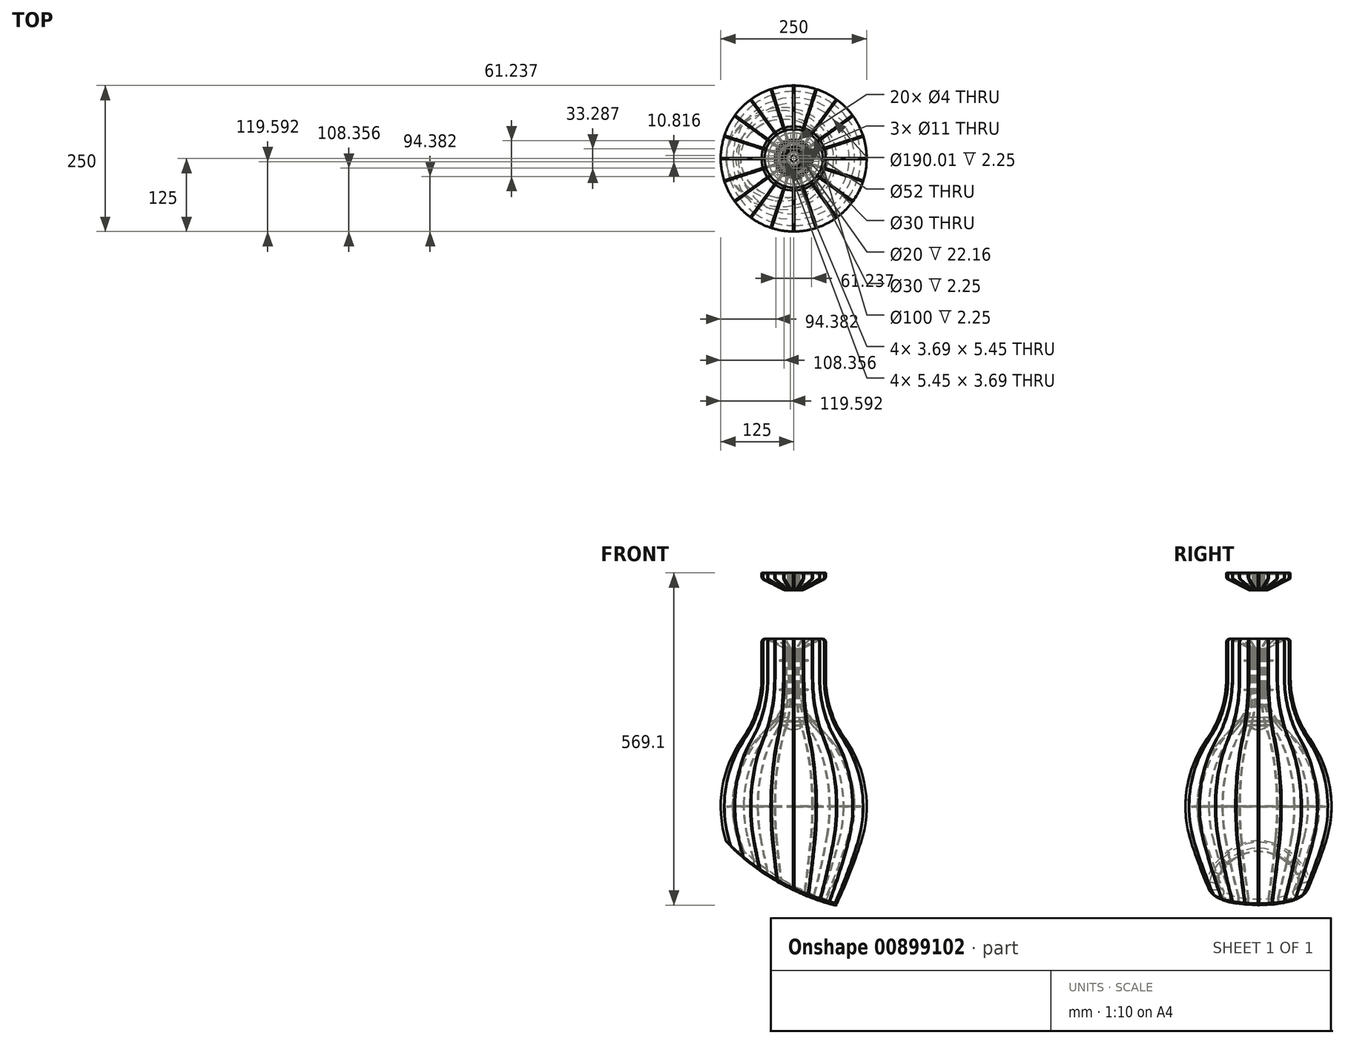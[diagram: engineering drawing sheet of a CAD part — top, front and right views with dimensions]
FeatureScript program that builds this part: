
annotation { "Feature Type Name" : "Feature", "Feature Type Description" : "" }
export const myFeature = defineFeature(function(context is Context, id is Id, definition is map)
    precondition{}
    {
        {
            assignVariable(context, id + "F0", {"variableType" : VariableType.LENGTH, "name" : "t", "lengthValue" : 2.25 * mm});
        }
        {
            var Q0;
            Q0=qCreatedBy(makeId("Front.planeOp"),FACE);
            var sketch = newSketch(context, id + "F1", { "sketchPlane" : qUnion([Q0])});
            skArc(sketch, "E0", {"start": v(-88.23, 115.57) * mm, "mid": v(-122.8, 29.63) * mm, "end": v(-114.93, -62.67) * mm});
            skArc(sketch, "E1", {"start": v(-88.23, 115.57) * mm, "mid": v(-63.5, 165.2) * mm, "end": v(-55, 220) * mm});
            skLineSegment(sketch, "E2", {"start": v(0, 0) * mm, "end": v(0, 200) * mm, "construction": true});
            skArc(sketch, "E3", {"start": v(-44.38, 134.72) * mm, "mid": v(-22.68, 164.2) * mm, "end": v(-15, 200) * mm});
            skArc(sketch, "E4", {"start": v(-44.38, 134.72) * mm, "mid": v(-98.19, 49.04) * mm, "end": v(-97.29, -52.12) * mm});
            skLineSegment(sketch, "E5", {"start": v(-55, 220) * mm, "end": v(-55, 290) * mm});
            skLineSegment(sketch, "E6", {"start": v(-55, 290) * mm, "end": v(-15, 270) * mm});
            skLineSegment(sketch, "E7", {"start": v(-15, 200) * mm, "end": v(-15, 270) * mm});
            skArc(sketch, "E8", {"start": v(-114.93, -62.67) * mm, "mid": v(-65.32, -185.14) * mm, "end": v(0, -300) * mm});
            skArc(sketch, "E9", {"start": v(-97.29, -52.12) * mm, "mid": v(-56.14, -159.57) * mm, "end": v(0, -260) * mm});
            skLineSegment(sketch, "E10", {"start": v(0, -300) * mm, "end": v(0, -260) * mm});
            skLineSegment(sketch, "E11", {"start": v(-10, 367.5) * mm, "end": v(-55, 390) * mm});
            skLineSegment(sketch, "E12", {"start": v(-55, 390) * mm, "end": v(-55, 400) * mm});
            skLineSegment(sketch, "E13", {"start": v(-55, 400) * mm, "end": v(-50, 400) * mm});
            skLineSegment(sketch, "E14", {"start": v(-10, 397.75) * mm, "end": v(-10, 367.5) * mm});
            skLineSegment(sketch, "E15", {"start": v(-50, 400) * mm, "end": v(-50, 397.75) * mm});
            skLineSegment(sketch, "E16", {"start": v(-50, 397.75) * mm, "end": v(-20, 397.75) * mm});
            skLineSegment(sketch, "E17", {"start": v(-20, 397.75) * mm, "end": v(-20, 400) * mm});
            skLineSegment(sketch, "E18.trimOffspring", {"start": v(-20, 400) * mm, "end": v(-15, 400) * mm});
            skLineSegment(sketch, "E19", {"start": v(-15, 400) * mm, "end": v(-15, 397.75) * mm});
            skLineSegment(sketch, "E20", {"start": v(-15, 397.75) * mm, "end": v(-10, 397.75) * mm});
            skPoint(sketch, "E21.orphan", {"position": v(-10, 400) * mm});
            skSolve(sketch);
        }
        {
            var Q0;
            Q0 = qSketchRegion(id + "F1", true);
            var Q1;
            Q1=sQuery(id+"F1.wireOp",EDGE,"E2");
            revolve(context, id + "F2", {"surfaceOperationType" : NewSurfaceOperationType.NEW, "entities" : qUnion([Q0]), "axis" : qUnion([Q1]), "revolveType" : RevolveType.FULL});
        }
        {
            var Q0;
            Q0=qCreatedBy(makeId("Front.planeOp"),FACE);
            var sketch = newSketch(context, id + "F3", { "sketchPlane" : qUnion([Q0])});
            skLineSegment(sketch, "E22.bottom", {"start": v(-115.8, -300) * mm, "end": v(72.5, -300) * mm});
            skLineSegment(sketch, "E22.left", {"start": v(72.5, -300) * mm, "end": v(72.5, -170) * mm});
            skLineSegment(sketch, "E22.right", {"start": v(-115.8, -300) * mm, "end": v(-115.8, -60) * mm});
            skLineSegment(sketch, "E23", {"start": v(0, 0) * mm, "end": v(0, -300) * mm, "construction": true});
            skPoint(sketch, "E24", {"position": v(-115.8, -60) * mm});
            skArc(sketch, "E25.converted", {"start": v(-115.8, -60) * mm, "mid": v(-29.3, -128.08) * mm, "end": v(72.5, -170) * mm});
            skLineSegment(sketch, "E26", {"start": v(72.5, -170) * mm, "end": v(-115.8, -170) * mm, "construction": true});
            skArc(sketch, "E27", {"start": v(0, -300) * mm, "mid": v(-65.32, -185.14) * mm, "end": v(-114.93, -62.67) * mm, "construction": true});
            skArc(sketch, "E28", {"start": v(114.93, -62.67) * mm, "mid": v(65.32, -185.14) * mm, "end": v(0, -300) * mm, "construction": true});
            skSolve(sketch);
        }
        {
            var Q0;
            Q0 = qSketchRegion(id + "F3", true);
            extrude(context, id + "F4", {"entities" : qUnion([Q0]), "operationType" : NewBodyOperationType.REMOVE, "depth" : 500 * mm, "offsetDistance" : 25 * mm, "symmetric" : true});
        }
        {
            var Q0;
            Q0=makeQuery(id+"F2.opRevolve","SWEPT_EDGE",EDGE,{"disambiguationData":[OSD([sQuery(id+"F1.wireOp",EDGE,"E5"),sQuery(id+"F1.wireOp",EDGE,"E6")])]});
            var Q1;
            Q1=makeQuery(id+"F2.opRevolve","SWEPT_EDGE",EDGE,{"disambiguationData":[OSD([sQuery(id+"F1.wireOp",EDGE,"E6"),sQuery(id+"F1.wireOp",EDGE,"E7")])]});
            var Q2;
            Q2=makeQuery(id+"F4.boolean.opBoolean","INTERSECT",EDGE,{"derivedFrom":[makeQuery(id+"F2.opRevolve","SWEPT_FACE",FACE,{"disambiguationData":[OSD([sQuery(id+"F1.wireOp",EDGE,"E8")])]}),makeQuery(id+"F4.opExtrude","SWEPT_FACE",FACE,{"disambiguationData":[OSD([sQuery(id+"F3.wireOp",EDGE,"E25.converted")])]})]});
            var Q3;
            Q3=makeQuery(id+"F4.boolean.opBoolean","INTERSECT",EDGE,{"derivedFrom":[makeQuery(id+"F2.opRevolve","SWEPT_FACE",FACE,{"disambiguationData":[OSD([sQuery(id+"F1.wireOp",EDGE,"E9")])]}),makeQuery(id+"F4.opExtrude","SWEPT_FACE",FACE,{"disambiguationData":[OSD([sQuery(id+"F3.wireOp",EDGE,"E25.converted")])]})]});
            var Q4;
            Q4=makeQuery(id+"F2.opRevolve","SWEPT_EDGE",EDGE,{"disambiguationData":[OSD([sQuery(id+"F1.wireOp",EDGE,"E11"),sQuery(id+"F1.wireOp",EDGE,"E14")])]});
            var Q5;
            Q5=makeQuery(id+"F2.opRevolve","SWEPT_EDGE",EDGE,{"disambiguationData":[OSD([sQuery(id+"F1.wireOp",EDGE,"E11"),sQuery(id+"F1.wireOp",EDGE,"E12")])]});
            fillet(context, id + "F5", {"entities" : qUnion([Q0, Q1, Q2, Q3, Q4, Q5]), "tangentPropagation" : true, "radius" : 5 * mm, "defaultsChanged" : false, "vertexSettings" : [], "allowEdgeOverflow" : false});
        }
        {
            var Q0;
            Q0=qCreatedBy(makeId("Front.planeOp"),FACE);
            var sketch = newSketch(context, id + "F6", { "sketchPlane" : qUnion([Q0])});
            skArc(sketch, "E29", {"start": v(-47.76, 286.38) * mm, "mid": v(-52.63, 286.16) * mm, "end": v(-55, 281.9) * mm});
            skArc(sketch, "E30", {"start": v(55, 281.9) * mm, "mid": v(52.63, 286.16) * mm, "end": v(47.76, 286.38) * mm});
            skLineSegment(sketch, "E31", {"start": v(55, 220) * mm, "end": v(55, 281.9) * mm});
            skLineSegment(sketch, "E32", {"start": v(-55, 281.9) * mm, "end": v(-55, 220) * mm});
            skArc(sketch, "E33", {"start": v(88.23, 115.57) * mm, "mid": v(63.5, 165.2) * mm, "end": v(55, 220) * mm});
            skArc(sketch, "E34", {"start": v(-55, 220) * mm, "mid": v(-63.5, 165.2) * mm, "end": v(-88.23, 115.57) * mm});
            skArc(sketch, "E35", {"start": v(88.23, 115.57) * mm, "mid": v(122.8, 29.63) * mm, "end": v(114.93, -62.67) * mm});
            skArc(sketch, "E36", {"start": v(-116.14, -58.88) * mm, "mid": v(-122.49, 31.6) * mm, "end": v(-88.23, 115.57) * mm});
            skArc(sketch, "E37", {"start": v(114.93, -62.67) * mm, "mid": v(96.03, -115) * mm, "end": v(74.26, -166.18) * mm});
            skArc(sketch, "E38", {"start": v(68.41, -168.92) * mm, "mid": v(71.84, -168.62) * mm, "end": v(74.26, -166.18) * mm});
            skArc(sketch, "E39", {"start": v(-99.56, -75.95) * mm, "mid": v(-107.36, -68.52) * mm, "end": v(-114.95, -60.88) * mm});
            skArc(sketch, "E40", {"start": v(68.41, -168.92) * mm, "mid": v(63.85, -167.67) * mm, "end": v(59.31, -166.36) * mm});
            skArc(sketch, "E41", {"start": v(56.2, -159.44) * mm, "mid": v(56.17, -163.61) * mm, "end": v(59.31, -166.36) * mm});
            skArc(sketch, "E42", {"start": v(-99.56, -75.95) * mm, "mid": v(-93.46, -76.5) * mm, "end": v(-91.41, -70.72) * mm});
            skArc(sketch, "E43", {"start": v(97.29, -52.12) * mm, "mid": v(78.67, -106.52) * mm, "end": v(56.2, -159.44) * mm});
            skArc(sketch, "E44", {"start": v(-91.41, -70.72) * mm, "mid": v(-94.4, -61.44) * mm, "end": v(-97.29, -52.12) * mm});
            skArc(sketch, "E45", {"start": v(44.38, 134.72) * mm, "mid": v(98.19, 49.04) * mm, "end": v(97.29, -52.12) * mm});
            skArc(sketch, "E46", {"start": v(-97.29, -52.12) * mm, "mid": v(-98.19, 49.04) * mm, "end": v(-44.38, 134.72) * mm});
            skArc(sketch, "E47", {"start": v(44.38, 134.72) * mm, "mid": v(22.68, 164.2) * mm, "end": v(15, 200) * mm});
            skArc(sketch, "E48", {"start": v(-15, 200) * mm, "mid": v(-22.68, 164.2) * mm, "end": v(-44.38, 134.72) * mm});
            skLineSegment(sketch, "E49", {"start": v(15, 200) * mm, "end": v(15, 266.9) * mm});
            skLineSegment(sketch, "E50", {"start": v(-15, 266.9) * mm, "end": v(-15, 200) * mm});
            skArc(sketch, "E51", {"start": v(-15, 266.9) * mm, "mid": v(-15.75, 269.54) * mm, "end": v(-17.76, 271.38) * mm});
            skArc(sketch, "E52", {"start": v(17.76, 271.38) * mm, "mid": v(15.75, 269.54) * mm, "end": v(15, 266.9) * mm});
            skLineSegment(sketch, "E53", {"start": v(-17.76, 271.38) * mm, "end": v(-47.76, 286.38) * mm});
            skLineSegment(sketch, "E54", {"start": v(47.76, 286.38) * mm, "end": v(17.76, 271.38) * mm});
            skArc(sketch, "E55", {"start": v(-116.14, -58.88) * mm, "mid": v(-115.66, -59.95) * mm, "end": v(-114.95, -60.88) * mm});
            skArc(sketch, "E56", {"start": v(-17.24, 371.12) * mm, "mid": v(-12.37, 371.34) * mm, "end": v(-10, 375.6) * mm});
            skLineSegment(sketch, "E57", {"start": v(-10, 375.6) * mm, "end": v(-10, 397.75) * mm});
            skLineSegment(sketch, "E58", {"start": v(-52.24, 388.62) * mm, "end": v(-17.24, 371.12) * mm});
            skArc(sketch, "E59", {"start": v(-55, 393.1) * mm, "mid": v(-54.25, 390.46) * mm, "end": v(-52.24, 388.62) * mm});
            skLineSegment(sketch, "E60", {"start": v(-55, 400) * mm, "end": v(-55, 393.1) * mm});
            skLineSegment(sketch, "E61", {"start": v(-50, 400) * mm, "end": v(-55, 400) * mm});
            skLineSegment(sketch, "E62", {"start": v(-20, 397.75) * mm, "end": v(-50, 397.75) * mm});
            skLineSegment(sketch, "E63", {"start": v(-15, 400) * mm, "end": v(-20, 400) * mm});
            skLineSegment(sketch, "E64", {"start": v(-10, 397.75) * mm, "end": v(-15, 397.75) * mm});
            skLineSegment(sketch, "E65", {"start": v(-15, 397.75) * mm, "end": v(-15, 400) * mm});
            skLineSegment(sketch, "E66", {"start": v(-20, 400) * mm, "end": v(-20, 397.75) * mm});
            skLineSegment(sketch, "E67", {"start": v(-50, 397.75) * mm, "end": v(-50, 400) * mm});
            skSolve(sketch);
        }
        {
            var Q0;
            Q0 = qSketchRegion(id + "F6", true);
            extrude(context, id + "F7", {"entities" : qUnion([Q0]), "depth" : getVariable(context, 't'), "offsetDistance" : 25 * mm, "symmetric" : true});
        }
        {
            var Q0;
            Q0=qCreatedBy(makeId("Front.planeOp"),FACE);
            var Q1;
            Q1=sQuery(id+"F3.wireOp",EDGE,"E23");
            cPlane(context, id + "F8", {"entities" : qUnion([Q0, Q1]), "cplaneType" : CPlaneType.LINE_ANGLE, "offset" : 25 * mm, "angle" : 18 * degree, "width" : 150 * mm, "height" : 150 * mm});
        }
        {
            var Q0;
            Q0=qCreatedBy(id+"F8.planeOp",FACE);
            var sketch = newSketch(context, id + "F9", { "sketchPlane" : qUnion([Q0])});
            skFitSpline(sketch, "E68", {"points": [v(-74.64, -165.34) * mm, v(-74.52, -165.6) * mm, v(-74.3, -165.99) * mm, v(-73.95, -166.45) * mm, v(-73.66, -166.78) * mm, v(-73.33, -167.08) * mm, v(-72.99, -167.35) * mm, v(-72.62, -167.59) * mm, v(-72.23, -167.8) * mm, v(-71.83, -167.97) * mm, v(-71.41, -168.1) * mm, v(-70.99, -168.2) * mm, v(-70.4, -168.28) * mm, v(-69.67, -168.28) * mm, v(-69.1, -168.19) * mm, v(-68.8, -168.1) * mm]});
            skFitSpline(sketch, "E69", {"points": [v(111.92, -69.42) * mm, v(112.28, -69.08) * mm, v(112.75, -68.51) * mm, v(113.24, -67.64) * mm, v(113.43, -67.18) * mm, v(113.5, -66.95) * mm]});
            skEllipticalArc(sketch, "E70", {});
            skEllipticalArc(sketch, "E71", {});
            skFitSpline(sketch, "E72", {"points": [v(89.43, -76.68) * mm, v(89.34, -76.94) * mm, v(89.2, -77.47) * mm, v(89.1, -78.3) * mm, v(89.13, -79.13) * mm, v(89.25, -79.8) * mm, v(89.4, -80.33) * mm, v(89.6, -80.85) * mm, v(89.86, -81.34) * mm, v(90.17, -81.8) * mm, v(90.44, -82.11) * mm, v(90.73, -82.4) * mm, v(91.04, -82.68) * mm, v(91.38, -82.92) * mm, v(91.74, -83.13) * mm, v(92.12, -83.3) * mm, v(92.5, -83.44) * mm, v(92.9, -83.55) * mm, v(93.31, -83.62) * mm, v(93.73, -83.65) * mm, v(94.14, -83.65) * mm, v(94.55, -83.61) * mm, v(95.1, -83.5) * mm, v(95.76, -83.3) * mm, v(96.5, -82.93) * mm, v(96.96, -82.6) * mm, v(97.17, -82.42) * mm]});
            skFitSpline(sketch, "E73", {"points": [v(-59.7, -165.6) * mm, v(-59.35, -165.5) * mm, v(-58.85, -165.3) * mm, v(-58.24, -164.92) * mm, v(-57.8, -164.58) * mm, v(-57.42, -164.2) * mm, v(-57.07, -163.8) * mm, v(-56.77, -163.34) * mm, v(-56.52, -162.86) * mm, v(-56.33, -162.36) * mm, v(-56.14, -161.65) * mm, v(-56.07, -160.94) * mm, v(-56.11, -160.21) * mm, v(-56.2, -159.68) * mm, v(-56.35, -159.16) * mm, v(-56.48, -158.83) * mm, v(-56.56, -158.66) * mm]});
            skArc(sketch, "E74", {"start": v(114.93, -62.67) * mm, "mid": v(114.22, -64.81) * mm, "end": v(113.5, -66.95) * mm});
            skArc(sketch, "E75", {"start": v(-74.64, -165.34) * mm, "mid": v(-96.2, -114.56) * mm, "end": v(-114.93, -62.67) * mm});
            skArc(sketch, "E76", {"start": v(88.23, 115.57) * mm, "mid": v(122.8, 29.63) * mm, "end": v(114.93, -62.67) * mm});
            skArc(sketch, "E77", {"start": v(-114.93, -62.67) * mm, "mid": v(-122.8, 29.63) * mm, "end": v(-88.23, 115.57) * mm});
            skArc(sketch, "E78", {"start": v(44.38, 134.72) * mm, "mid": v(98.19, 49.04) * mm, "end": v(97.29, -52.12) * mm});
            skArc(sketch, "E79", {"start": v(-97.29, -52.12) * mm, "mid": v(-98.19, 49.04) * mm, "end": v(-44.38, 134.72) * mm});
            skArc(sketch, "E80", {"start": v(97.29, -52.12) * mm, "mid": v(93.46, -64.43) * mm, "end": v(89.43, -76.68) * mm});
            skArc(sketch, "E81", {"start": v(-56.56, -158.66) * mm, "mid": v(-78.83, -106.12) * mm, "end": v(-97.29, -52.12) * mm});
            skArc(sketch, "E82", {"start": v(88.23, 115.57) * mm, "mid": v(63.5, 165.2) * mm, "end": v(55, 220) * mm});
            skArc(sketch, "E83", {"start": v(-55, 220) * mm, "mid": v(-63.5, 165.2) * mm, "end": v(-88.23, 115.57) * mm});
            skLineSegment(sketch, "E84", {"start": v(55, 220) * mm, "end": v(55, 281.9) * mm});
            skLineSegment(sketch, "E85", {"start": v(-55, 281.9) * mm, "end": v(-55, 220) * mm});
            skArc(sketch, "E86", {"start": v(-47.76, 286.38) * mm, "mid": v(-52.63, 286.16) * mm, "end": v(-55, 281.9) * mm});
            skArc(sketch, "E87", {"start": v(55, 281.9) * mm, "mid": v(52.63, 286.16) * mm, "end": v(47.76, 286.38) * mm});
            skLineSegment(sketch, "E88", {"start": v(-17.76, 271.38) * mm, "end": v(-47.76, 286.38) * mm});
            skLineSegment(sketch, "E89", {"start": v(47.76, 286.38) * mm, "end": v(17.76, 271.38) * mm});
            skArc(sketch, "E90", {"start": v(-15, 266.9) * mm, "mid": v(-15.75, 269.54) * mm, "end": v(-17.76, 271.38) * mm});
            skArc(sketch, "E91", {"start": v(17.76, 271.38) * mm, "mid": v(15.75, 269.54) * mm, "end": v(15, 266.9) * mm});
            skLineSegment(sketch, "E92", {"start": v(15, 200) * mm, "end": v(15, 266.9) * mm});
            skLineSegment(sketch, "E93", {"start": v(-15, 266.9) * mm, "end": v(-15, 200) * mm});
            skArc(sketch, "E94", {"start": v(44.38, 134.72) * mm, "mid": v(22.68, 164.2) * mm, "end": v(15, 200) * mm});
            skArc(sketch, "E95", {"start": v(-15, 200) * mm, "mid": v(-22.68, 164.2) * mm, "end": v(-44.38, 134.72) * mm});
            const initialGuessF9  = {"E70": [-0.18134494701990392, 0.217305327537415, 1, 0, 0.4205848896953069, 0.4, 4.98326227178671, 5.0058128826202495], "E71": [-0.18134494701990392, 0.217305327537415, 1, 0, 0.4205848896953069, 0.4, 5.436156316925889, 5.4839668003792745]};
            skSetInitialGuess(sketch, initialGuessF9);
            skSolve(sketch);
        }
        {
            var Q0;
            Q0 = qSketchRegion(id + "F9", true);
            extrude(context, id + "F10", {"entities" : qUnion([Q0]), "depth" : getVariable(context, 't'), "offsetDistance" : 25 * mm, "symmetric" : true});
        }
        {
            var Q0;
            Q0=qCreatedBy(makeId("Front.planeOp"),FACE);
            var Q1;
            Q1=sQuery(id+"F3.wireOp",EDGE,"E23");
            cPlane(context, id + "F11", {"entities" : qUnion([Q0, Q1]), "cplaneType" : CPlaneType.LINE_ANGLE, "offset" : 25 * mm, "angle" : 36 * degree, "width" : 150 * mm, "height" : 150 * mm});
        }
        {
            var Q0;
            Q0=qCreatedBy(id+"F11.planeOp",FACE);
            var sketch = newSketch(context, id + "F12", { "sketchPlane" : qUnion([Q0])});
            skArc(sketch, "E96", {"start": v(-47.76, 286.38) * mm, "mid": v(-52.63, 286.16) * mm, "end": v(-55, 281.9) * mm});
            skArc(sketch, "E97", {"start": v(55, 281.9) * mm, "mid": v(52.63, 286.16) * mm, "end": v(47.76, 286.38) * mm});
            skLineSegment(sketch, "E98", {"start": v(55, 220) * mm, "end": v(55, 281.9) * mm});
            skLineSegment(sketch, "E99", {"start": v(-55, 281.9) * mm, "end": v(-55, 220) * mm});
            skArc(sketch, "E100", {"start": v(88.23, 115.57) * mm, "mid": v(63.5, 165.2) * mm, "end": v(55, 220) * mm});
            skArc(sketch, "E101", {"start": v(-55, 220) * mm, "mid": v(-63.5, 165.2) * mm, "end": v(-88.23, 115.57) * mm});
            skArc(sketch, "E102", {"start": v(88.23, 115.57) * mm, "mid": v(122.8, 29.63) * mm, "end": v(114.93, -62.67) * mm});
            skArc(sketch, "E103", {"start": v(-114.93, -62.67) * mm, "mid": v(-122.8, 29.63) * mm, "end": v(-88.23, 115.57) * mm});
            skArc(sketch, "E104", {"start": v(114.93, -62.67) * mm, "mid": v(111, -74.3) * mm, "end": v(106.95, -85.88) * mm});
            skArc(sketch, "E105", {"start": v(-75.84, -162.71) * mm, "mid": v(-96.73, -113.22) * mm, "end": v(-114.93, -62.67) * mm});
            skFitSpline(sketch, "E106", {"points": [v(-75.84, -162.71) * mm, v(-75.72, -162.98) * mm, v(-75.5, -163.36) * mm, v(-75.16, -163.83) * mm, v(-74.87, -164.16) * mm, v(-74.55, -164.46) * mm, v(-74.2, -164.73) * mm, v(-73.85, -164.98) * mm, v(-73.46, -165.2) * mm, v(-73.06, -165.37) * mm, v(-72.64, -165.5) * mm, v(-72.22, -165.61) * mm, v(-71.79, -165.68) * mm, v(-71.35, -165.71) * mm, v(-70.77, -165.7) * mm, v(-70.34, -165.64) * mm, v(-70.05, -165.57) * mm]});
            skFitSpline(sketch, "E107", {"points": [v(104.37, -89.28) * mm, v(104.68, -89.08) * mm, v(105.1, -88.74) * mm, v(105.6, -88.21) * mm, v(106.05, -87.65) * mm, v(106.53, -86.9) * mm, v(106.83, -86.23) * mm, v(106.95, -85.88) * mm]});
            skEllipticalArc(sketch, "E108", {});
            skEllipticalArc(sketch, "E109", {});
            skFitSpline(sketch, "E110", {"points": [v(84.35, -91.22) * mm, v(84.17, -91.73) * mm, v(83.98, -92.51) * mm, v(83.92, -93.45) * mm, v(83.94, -94) * mm, v(83.99, -94.53) * mm, v(84.11, -95.18) * mm, v(84.32, -95.82) * mm, v(84.55, -96.31) * mm, v(84.75, -96.66) * mm, v(84.97, -97) * mm, v(85.23, -97.31) * mm, v(85.51, -97.6) * mm, v(85.82, -97.87) * mm, v(86.14, -98.1) * mm, v(86.5, -98.3) * mm, v(86.87, -98.48) * mm, v(87.25, -98.6) * mm, v(87.64, -98.7) * mm, v(88.05, -98.76) * mm, v(88.45, -98.77) * mm, v(88.85, -98.75) * mm, v(89.26, -98.7) * mm, v(89.79, -98.58) * mm, v(90.42, -98.35) * mm, v(90.9, -98.1) * mm, v(91.13, -97.95) * mm]});
            skFitSpline(sketch, "E111", {"points": [v(-60.9, -163.25) * mm, v(-60.54, -163.16) * mm, v(-59.86, -162.9) * mm, v(-59.1, -162.38) * mm, v(-58.56, -161.88) * mm, v(-58.2, -161.45) * mm, v(-57.9, -161) * mm, v(-57.65, -160.51) * mm, v(-57.45, -160) * mm, v(-57.3, -159.46) * mm, v(-57.22, -158.92) * mm, v(-57.2, -158.37) * mm, v(-57.23, -157.82) * mm, v(-57.32, -157.28) * mm, v(-57.47, -156.75) * mm, v(-57.6, -156.4) * mm, v(-57.69, -156.24) * mm]});
            skArc(sketch, "E112", {"start": v(97.29, -52.12) * mm, "mid": v(91.07, -71.76) * mm, "end": v(84.35, -91.22) * mm});
            skArc(sketch, "E113", {"start": v(-57.69, -156.24) * mm, "mid": v(-79.3, -104.87) * mm, "end": v(-97.29, -52.12) * mm});
            skArc(sketch, "E114", {"start": v(44.38, 134.72) * mm, "mid": v(98.19, 49.04) * mm, "end": v(97.29, -52.12) * mm});
            skArc(sketch, "E115", {"start": v(-97.29, -52.12) * mm, "mid": v(-98.19, 49.04) * mm, "end": v(-44.38, 134.72) * mm});
            skArc(sketch, "E116", {"start": v(44.38, 134.72) * mm, "mid": v(22.68, 164.2) * mm, "end": v(15, 200) * mm});
            skArc(sketch, "E117", {"start": v(-15, 200) * mm, "mid": v(-22.68, 164.2) * mm, "end": v(-44.38, 134.72) * mm});
            skLineSegment(sketch, "E118", {"start": v(15, 200) * mm, "end": v(15, 266.9) * mm});
            skLineSegment(sketch, "E119", {"start": v(-15, 266.9) * mm, "end": v(-15, 200) * mm});
            skLineSegment(sketch, "E120", {"start": v(-17.76, 271.38) * mm, "end": v(-47.76, 286.38) * mm});
            skLineSegment(sketch, "E121", {"start": v(47.76, 286.38) * mm, "end": v(17.76, 271.38) * mm});
            skArc(sketch, "E122", {"start": v(-15, 266.9) * mm, "mid": v(-15.75, 269.54) * mm, "end": v(-17.76, 271.38) * mm});
            skArc(sketch, "E123", {"start": v(17.76, 271.38) * mm, "mid": v(15.75, 269.54) * mm, "end": v(15, 266.9) * mm});
            const initialGuessF12  = {"E108": [-0.21318377087211882, 0.217305327537415, 1, 0, 0.4944271909999159, 0.4, 5.0060869802314505, 5.025477783736927], "E109": [-0.21318377087211882, 0.217305327537415, 1, 0, 0.4944271909999159, 0.4, 5.375399704778273, 5.409850527573943]};
            skSetInitialGuess(sketch, initialGuessF12);
            skSolve(sketch);
        }
        {
            var Q0;
            Q0 = qSketchRegion(id + "F12", true);
            extrude(context, id + "F13", {"entities" : qUnion([Q0]), "depth" : getVariable(context, 't'), "offsetDistance" : 25 * mm, "symmetric" : true});
        }
        {
            var Q0;
            Q0=qCreatedBy(makeId("Front.planeOp"),FACE);
            var Q1;
            Q1=sQuery(id+"F3.wireOp",EDGE,"E23");
            cPlane(context, id + "F14", {"entities" : qUnion([Q0, Q1]), "cplaneType" : CPlaneType.LINE_ANGLE, "offset" : 25 * mm, "angle" : 54 * degree, "width" : 150 * mm, "height" : 150 * mm});
        }
        {
            var Q0;
            Q0=qCreatedBy(id+"F14.planeOp",FACE);
            var sketch = newSketch(context, id + "F15", { "sketchPlane" : qUnion([Q0])});
            skArc(sketch, "E124", {"start": v(-15, 266.9) * mm, "mid": v(-15.75, 269.54) * mm, "end": v(-17.76, 271.38) * mm});
            skArc(sketch, "E125", {"start": v(17.76, 271.38) * mm, "mid": v(15.75, 269.54) * mm, "end": v(15, 266.9) * mm});
            skLineSegment(sketch, "E126", {"start": v(15, 200) * mm, "end": v(15, 266.9) * mm});
            skLineSegment(sketch, "E127", {"start": v(-15, 266.9) * mm, "end": v(-15, 200) * mm});
            skLineSegment(sketch, "E128", {"start": v(-17.76, 271.38) * mm, "end": v(-47.76, 286.38) * mm});
            skLineSegment(sketch, "E129", {"start": v(47.76, 286.38) * mm, "end": v(17.76, 271.38) * mm});
            skArc(sketch, "E130", {"start": v(-47.76, 286.38) * mm, "mid": v(-52.63, 286.16) * mm, "end": v(-55, 281.9) * mm});
            skArc(sketch, "E131", {"start": v(55, 281.9) * mm, "mid": v(52.63, 286.16) * mm, "end": v(47.76, 286.38) * mm});
            skLineSegment(sketch, "E132", {"start": v(55, 220) * mm, "end": v(55, 281.9) * mm});
            skLineSegment(sketch, "E133", {"start": v(-55, 281.9) * mm, "end": v(-55, 220) * mm});
            skArc(sketch, "E134", {"start": v(88.23, 115.57) * mm, "mid": v(63.5, 165.2) * mm, "end": v(55, 220) * mm});
            skArc(sketch, "E135", {"start": v(-55, 220) * mm, "mid": v(-63.5, 165.2) * mm, "end": v(-88.23, 115.57) * mm});
            skArc(sketch, "E136", {"start": v(88.23, 115.57) * mm, "mid": v(122.8, 29.63) * mm, "end": v(114.93, -62.67) * mm});
            skArc(sketch, "E137", {"start": v(-114.93, -62.67) * mm, "mid": v(-122.8, 29.63) * mm, "end": v(-88.23, 115.57) * mm});
            skArc(sketch, "E138", {"start": v(114.93, -62.67) * mm, "mid": v(107.28, -84.96) * mm, "end": v(99.11, -107.05) * mm});
            skArc(sketch, "E139", {"start": v(-77.98, -157.97) * mm, "mid": v(-97.67, -110.8) * mm, "end": v(-114.93, -62.67) * mm});
            skFitSpline(sketch, "E140", {"points": [v(-77.98, -157.97) * mm, v(-77.86, -158.24) * mm, v(-77.58, -158.74) * mm, v(-77.14, -159.31) * mm, v(-76.72, -159.73) * mm, v(-76.4, -160) * mm, v(-76.04, -160.26) * mm, v(-75.67, -160.48) * mm, v(-75.27, -160.67) * mm, v(-74.74, -160.88) * mm, v(-74.18, -161.02) * mm, v(-73.6, -161.08) * mm, v(-73.02, -161.1) * mm, v(-72.59, -161.05) * mm, v(-72.3, -160.99) * mm]});
            skFitSpline(sketch, "E141", {"points": [v(95.5, -110.94) * mm, v(95.92, -110.76) * mm, v(96.5, -110.43) * mm, v(97.21, -109.86) * mm, v(97.86, -109.21) * mm, v(98.4, -108.49) * mm, v(98.85, -107.68) * mm, v(99.03, -107.26) * mm, v(99.11, -107.05) * mm]});
            skEllipticalArc(sketch, "E142", {});
            skEllipticalArc(sketch, "E143", {});
            skFitSpline(sketch, "E144", {"points": [v(78.01, -108.24) * mm, v(77.83, -108.71) * mm, v(77.63, -109.44) * mm, v(77.51, -110.43) * mm, v(77.5, -111.2) * mm, v(77.58, -111.94) * mm, v(77.75, -112.67) * mm, v(78.02, -113.38) * mm, v(78.38, -114.04) * mm, v(78.84, -114.65) * mm, v(79.3, -115.07) * mm, v(79.71, -115.36) * mm, v(80.16, -115.61) * mm, v(80.73, -115.84) * mm, v(81.49, -116) * mm, v(82.24, -116) * mm, v(83, -115.9) * mm, v(83.48, -115.74) * mm, v(83.71, -115.65) * mm]});
            skFitSpline(sketch, "E145", {"points": [v(-63.04, -159.08) * mm, v(-62.66, -159) * mm, v(-62.13, -158.82) * mm, v(-61.46, -158.45) * mm, v(-61, -158.12) * mm, v(-60.59, -157.74) * mm, v(-60.08, -157.16) * mm, v(-59.7, -156.52) * mm, v(-59.42, -155.8) * mm, v(-59.27, -155.26) * mm, v(-59.19, -154.7) * mm, v(-59.15, -153.94) * mm, v(-59.26, -153) * mm, v(-59.5, -152.28) * mm, v(-59.66, -151.94) * mm]});
            skArc(sketch, "E146", {"start": v(97.29, -52.12) * mm, "mid": v(88.17, -80.36) * mm, "end": v(78.01, -108.24) * mm});
            skArc(sketch, "E147", {"start": v(-59.66, -151.94) * mm, "mid": v(-80.14, -102.66) * mm, "end": v(-97.29, -52.12) * mm});
            skArc(sketch, "E148", {"start": v(44.38, 134.72) * mm, "mid": v(98.19, 49.04) * mm, "end": v(97.29, -52.12) * mm});
            skArc(sketch, "E149", {"start": v(-97.29, -52.12) * mm, "mid": v(-98.19, 49.04) * mm, "end": v(-44.38, 134.72) * mm});
            skArc(sketch, "E150", {"start": v(44.38, 134.72) * mm, "mid": v(22.68, 164.2) * mm, "end": v(15, 200) * mm});
            skArc(sketch, "E151", {"start": v(-15, 200) * mm, "mid": v(-22.68, 164.2) * mm, "end": v(-44.38, 134.72) * mm});
            const initialGuessF15  = {"E142": [-0.2934222879662535, 0.217305327537415, 1, 0, 0.6805206466816319, 0.4, 5.043329519341684, 5.05775691142949], "E143": [-0.2934222879662535, 0.217305327537415, 1, 0, 0.6805206466816319, 0.4, 5.299776253378362, 5.320715593614243]};
            skSetInitialGuess(sketch, initialGuessF15);
            skSolve(sketch);
        }
        {
            var Q0;
            Q0 = qSketchRegion(id + "F15", true);
            extrude(context, id + "F16", {"entities" : qUnion([Q0]), "depth" : getVariable(context, 't'), "offsetDistance" : 25 * mm, "symmetric" : true});
        }
        {
            var Q0;
            Q0=qCreatedBy(makeId("Front.planeOp"),FACE);
            var Q1;
            Q1=sQuery(id+"F3.wireOp",EDGE,"E23");
            cPlane(context, id + "F17", {"entities" : qUnion([Q0, Q1]), "cplaneType" : CPlaneType.LINE_ANGLE, "offset" : 25 * mm, "angle" : 72 * degree, "width" : 150 * mm, "height" : 150 * mm});
        }
        {
            var Q0;
            Q0=qCreatedBy(id+"F17.planeOp",FACE);
            var sketch = newSketch(context, id + "F18", { "sketchPlane" : qUnion([Q0])});
            skLineSegment(sketch, "E152", {"start": v(-17.76, 271.38) * mm, "end": v(-47.76, 286.38) * mm});
            skLineSegment(sketch, "E153", {"start": v(47.76, 286.38) * mm, "end": v(17.76, 271.38) * mm});
            skArc(sketch, "E154", {"start": v(-15, 266.9) * mm, "mid": v(-15.75, 269.54) * mm, "end": v(-17.76, 271.38) * mm});
            skArc(sketch, "E155", {"start": v(17.76, 271.38) * mm, "mid": v(15.75, 269.54) * mm, "end": v(15, 266.9) * mm});
            skArc(sketch, "E156", {"start": v(-47.76, 286.38) * mm, "mid": v(-52.63, 286.16) * mm, "end": v(-55, 281.9) * mm});
            skArc(sketch, "E157", {"start": v(55, 281.9) * mm, "mid": v(52.63, 286.16) * mm, "end": v(47.76, 286.38) * mm});
            skLineSegment(sketch, "E158", {"start": v(55, 220) * mm, "end": v(55, 281.9) * mm});
            skLineSegment(sketch, "E159", {"start": v(-55, 281.9) * mm, "end": v(-55, 220) * mm});
            skArc(sketch, "E160", {"start": v(88.23, 115.57) * mm, "mid": v(63.5, 165.2) * mm, "end": v(55, 220) * mm});
            skArc(sketch, "E161", {"start": v(-55, 220) * mm, "mid": v(-63.5, 165.2) * mm, "end": v(-88.23, 115.57) * mm});
            skArc(sketch, "E162", {"start": v(88.23, 115.57) * mm, "mid": v(122.8, 29.63) * mm, "end": v(114.93, -62.67) * mm});
            skArc(sketch, "E163", {"start": v(-114.93, -62.67) * mm, "mid": v(-122.8, 29.63) * mm, "end": v(-88.23, 115.57) * mm});
            skArc(sketch, "E164", {"start": v(114.93, -62.67) * mm, "mid": v(103.9, -94.3) * mm, "end": v(91.82, -125.55) * mm});
            skArc(sketch, "E165", {"start": v(-81.24, -150.61) * mm, "mid": v(-99.12, -107.04) * mm, "end": v(-114.93, -62.67) * mm});
            skFitSpline(sketch, "E166", {"points": [v(-81.24, -150.61) * mm, v(-81.12, -150.87) * mm, v(-80.86, -151.37) * mm, v(-80.44, -151.94) * mm, v(-80.05, -152.36) * mm, v(-79.63, -152.75) * mm, v(-79.06, -153.17) * mm, v(-78.3, -153.56) * mm, v(-77.62, -153.78) * mm, v(-77.06, -153.88) * mm, v(-76.5, -153.94) * mm, v(-76.07, -153.92) * mm, v(-75.78, -153.89) * mm]});
            skFitSpline(sketch, "E167", {"points": [v(87.34, -129.42) * mm, v(87.6, -129.37) * mm, v(88.1, -129.24) * mm, v(88.8, -128.94) * mm, v(89.47, -128.54) * mm, v(90.07, -128.07) * mm, v(90.62, -127.51) * mm, v(91.1, -126.9) * mm, v(91.5, -126.25) * mm, v(91.72, -125.79) * mm, v(91.82, -125.55) * mm]});
            skEllipticalArc(sketch, "E168", {});
            skEllipticalArc(sketch, "E169", {});
            skFitSpline(sketch, "E170", {"points": [v(71.87, -123.68) * mm, v(71.7, -124.1) * mm, v(71.5, -124.77) * mm, v(71.37, -125.67) * mm, v(71.34, -126.37) * mm, v(71.38, -127.06) * mm, v(71.5, -127.73) * mm, v(71.7, -128.4) * mm, v(72, -129.03) * mm, v(72.36, -129.61) * mm, v(72.82, -130.15) * mm, v(73.26, -130.52) * mm, v(73.65, -130.77) * mm, v(74.06, -131) * mm, v(74.49, -131.16) * mm, v(74.93, -131.27) * mm, v(75.4, -131.35) * mm, v(75.97, -131.38) * mm, v(76.43, -131.33) * mm, v(76.66, -131.3) * mm]});
            skFitSpline(sketch, "E171", {"points": [v(-66.27, -152.7) * mm, v(-65.88, -152.64) * mm, v(-65.3, -152.5) * mm, v(-64.58, -152.15) * mm, v(-64.08, -151.83) * mm, v(-63.63, -151.45) * mm, v(-63.22, -151) * mm, v(-62.88, -150.52) * mm, v(-62.6, -150) * mm, v(-62.37, -149.44) * mm, v(-62.22, -148.87) * mm, v(-62.13, -148.27) * mm, v(-62.1, -147.68) * mm, v(-62.14, -147.09) * mm, v(-62.27, -146.3) * mm, v(-62.45, -145.73) * mm, v(-62.62, -145.37) * mm]});
            skArc(sketch, "E172", {"start": v(44.38, 134.72) * mm, "mid": v(98.19, 49.04) * mm, "end": v(97.29, -52.12) * mm});
            skArc(sketch, "E173", {"start": v(-97.29, -52.12) * mm, "mid": v(-98.19, 49.04) * mm, "end": v(-44.38, 134.72) * mm});
            skArc(sketch, "E174", {"start": v(97.29, -52.12) * mm, "mid": v(85.43, -88.2) * mm, "end": v(71.87, -123.68) * mm});
            skArc(sketch, "E175", {"start": v(-62.62, -145.37) * mm, "mid": v(-81.4, -99.29) * mm, "end": v(-97.29, -52.12) * mm});
            skArc(sketch, "E176", {"start": v(44.38, 134.72) * mm, "mid": v(22.68, 164.2) * mm, "end": v(15, 200) * mm});
            skArc(sketch, "E177", {"start": v(-15, 200) * mm, "mid": v(-22.68, 164.2) * mm, "end": v(-44.38, 134.72) * mm});
            skLineSegment(sketch, "E178", {"start": v(15, 200) * mm, "end": v(15, 266.9) * mm});
            skLineSegment(sketch, "E179", {"start": v(-15, 266.9) * mm, "end": v(-15, 200) * mm});
            const initialGuessF18  = {"E168": [-0.5581223579930769, 0.217305327537415, 1, 0, 1.2944271909999157, 0.4, 5.094229930988491, 5.10215609820481], "E169": [-0.5581223579930769, 0.217305327537415, 1, 0, 1.2944271909999157, 0.4, 5.22493701014662, 5.23443071205651]};
            skSetInitialGuess(sketch, initialGuessF18);
            skSolve(sketch);
        }
        {
            var Q0;
            Q0 = qSketchRegion(id + "F18", true);
            extrude(context, id + "F19", {"entities" : qUnion([Q0]), "depth" : getVariable(context, 't'), "offsetDistance" : 25 * mm, "symmetric" : true});
        }
        {
            var Q0;
            Q0=qCreatedBy(makeId("Front.planeOp"),FACE);
            var Q1;
            Q1=sQuery(id+"F3.wireOp",EDGE,"E23");
            cPlane(context, id + "F20", {"entities" : qUnion([Q0, Q1]), "cplaneType" : CPlaneType.LINE_ANGLE, "offset" : 25 * mm, "angle" : 90 * degree, "width" : 150 * mm, "height" : 150 * mm});
        }
        {
            var Q0;
            Q0=qCreatedBy(id+"F20.planeOp",FACE);
            var sketch = newSketch(context, id + "F21", { "sketchPlane" : qUnion([Q0])});
            skFitSpline(sketch, "E180", {"points": [v(66.67, -136.08) * mm, v(66.5, -136.47) * mm, v(66.31, -137.08) * mm, v(66.18, -137.92) * mm, v(66.13, -138.77) * mm, v(66.21, -139.6) * mm, v(66.45, -140.43) * mm, v(66.69, -141.02) * mm, v(66.95, -141.48) * mm, v(67.2, -141.82) * mm, v(67.47, -142.16) * mm, v(67.84, -142.53) * mm, v(68.35, -142.91) * mm, v(68.92, -143.22) * mm, v(69.52, -143.44) * mm, v(70.14, -143.57) * mm, v(70.57, -143.6) * mm, v(70.79, -143.6) * mm]});
            skFitSpline(sketch, "E181", {"points": [v(-70.79, -143.6) * mm, v(-70.57, -143.6) * mm, v(-70.15, -143.57) * mm, v(-69.53, -143.44) * mm, v(-68.92, -143.22) * mm, v(-68.37, -142.92) * mm, v(-67.85, -142.54) * mm, v(-67.4, -142.1) * mm, v(-67.01, -141.58) * mm, v(-66.7, -141.03) * mm, v(-66.45, -140.44) * mm, v(-66.22, -139.62) * mm, v(-66.13, -138.77) * mm, v(-66.18, -137.92) * mm, v(-66.28, -137.3) * mm, v(-66.44, -136.68) * mm, v(-66.59, -136.28) * mm, v(-66.67, -136.08) * mm]});
            skLineSegment(sketch, "E182", {"start": v(-70.79, -143.6) * mm, "end": v(-80.74, -143.6) * mm});
            skLineSegment(sketch, "E183", {"start": v(80.74, -143.6) * mm, "end": v(70.79, -143.6) * mm});
            skFitSpline(sketch, "E184", {"points": [v(-85.81, -140) * mm, v(-85.6, -140.52) * mm, v(-85.18, -141.22) * mm, v(-84.44, -142.05) * mm, v(-83.82, -142.58) * mm, v(-83.24, -142.94) * mm, v(-82.74, -143.18) * mm, v(-82.23, -143.38) * mm, v(-81.57, -143.55) * mm, v(-81.02, -143.6) * mm, v(-80.74, -143.6) * mm]});
            skFitSpline(sketch, "E185", {"points": [v(80.74, -143.6) * mm, v(81.02, -143.6) * mm, v(81.56, -143.55) * mm, v(82.22, -143.38) * mm, v(82.74, -143.18) * mm, v(83.23, -142.95) * mm, v(83.7, -142.65) * mm, v(84.13, -142.31) * mm, v(84.53, -141.94) * mm, v(84.99, -141.44) * mm, v(85.46, -140.75) * mm, v(85.7, -140.26) * mm, v(85.81, -140) * mm]});
            skArc(sketch, "E186", {"start": v(114.93, -62.67) * mm, "mid": v(101.17, -101.64) * mm, "end": v(85.81, -140) * mm});
            skArc(sketch, "E187", {"start": v(-85.81, -140) * mm, "mid": v(-101.17, -101.64) * mm, "end": v(-114.93, -62.67) * mm});
            skArc(sketch, "E188", {"start": v(88.23, 115.57) * mm, "mid": v(122.8, 29.63) * mm, "end": v(114.93, -62.67) * mm});
            skArc(sketch, "E189", {"start": v(-114.93, -62.67) * mm, "mid": v(-122.8, 29.63) * mm, "end": v(-88.23, 115.57) * mm});
            skArc(sketch, "E190", {"start": v(44.38, 134.72) * mm, "mid": v(98.19, 49.04) * mm, "end": v(97.29, -52.12) * mm});
            skArc(sketch, "E191", {"start": v(-97.29, -52.12) * mm, "mid": v(-98.19, 49.04) * mm, "end": v(-44.38, 134.72) * mm});
            skArc(sketch, "E192", {"start": v(97.29, -52.12) * mm, "mid": v(83.15, -94.53) * mm, "end": v(66.67, -136.08) * mm});
            skArc(sketch, "E193", {"start": v(-66.67, -136.08) * mm, "mid": v(-83.15, -94.53) * mm, "end": v(-97.29, -52.12) * mm});
            skArc(sketch, "E194", {"start": v(44.38, 134.72) * mm, "mid": v(22.68, 164.2) * mm, "end": v(15, 200) * mm});
            skArc(sketch, "E195", {"start": v(-15, 200) * mm, "mid": v(-22.68, 164.2) * mm, "end": v(-44.38, 134.72) * mm});
            skLineSegment(sketch, "E196", {"start": v(15, 200) * mm, "end": v(15, 266.9) * mm});
            skLineSegment(sketch, "E197", {"start": v(-15, 266.9) * mm, "end": v(-15, 200) * mm});
            skArc(sketch, "E198", {"start": v(-15, 266.9) * mm, "mid": v(-15.75, 269.54) * mm, "end": v(-17.76, 271.38) * mm});
            skArc(sketch, "E199", {"start": v(17.76, 271.38) * mm, "mid": v(15.75, 269.54) * mm, "end": v(15, 266.9) * mm});
            skLineSegment(sketch, "E200", {"start": v(-17.76, 271.38) * mm, "end": v(-47.76, 286.38) * mm});
            skLineSegment(sketch, "E201", {"start": v(47.76, 286.38) * mm, "end": v(17.76, 271.38) * mm});
            skArc(sketch, "E202", {"start": v(-47.76, 286.38) * mm, "mid": v(-52.63, 286.16) * mm, "end": v(-55, 281.9) * mm});
            skArc(sketch, "E203", {"start": v(55, 281.9) * mm, "mid": v(52.63, 286.16) * mm, "end": v(47.76, 286.38) * mm});
            skLineSegment(sketch, "E204", {"start": v(55, 220) * mm, "end": v(55, 281.9) * mm});
            skLineSegment(sketch, "E205", {"start": v(-55, 281.9) * mm, "end": v(-55, 220) * mm});
            skArc(sketch, "E206", {"start": v(88.23, 115.57) * mm, "mid": v(63.5, 165.2) * mm, "end": v(55, 220) * mm});
            skArc(sketch, "E207", {"start": v(-55, 220) * mm, "mid": v(-63.5, 165.2) * mm, "end": v(-88.23, 115.57) * mm});
            skSolve(sketch);
        }
        {
            var Q0;
            Q0 = qSketchRegion(id + "F21", true);
            extrude(context, id + "F22", {"entities" : qUnion([Q0]), "depth" : getVariable(context, 't'), "offsetDistance" : 25 * mm, "symmetric" : true});
        }
        {
            var Q0;
            Q0=qCreatedBy(makeId("Front.planeOp"),FACE);
            var Q1;
            Q1=sQuery(id+"F3.wireOp",EDGE,"E23");
            cPlane(context, id + "F23", {"entities" : qUnion([Q0, Q1]), "cplaneType" : CPlaneType.LINE_ANGLE, "offset" : 25 * mm, "angle" : 108 * degree, "width" : 150 * mm, "height" : 150 * mm});
        }
        {
            var Q0;
            Q0=qCreatedBy(id+"F23.planeOp",FACE);
            var sketch = newSketch(context, id + "F24", { "sketchPlane" : qUnion([Q0])});
            skArc(sketch, "E208", {"start": v(-15, 266.9) * mm, "mid": v(-15.75, 269.54) * mm, "end": v(-17.76, 271.38) * mm});
            skArc(sketch, "E209", {"start": v(17.76, 271.38) * mm, "mid": v(15.75, 269.54) * mm, "end": v(15, 266.9) * mm});
            skLineSegment(sketch, "E210", {"start": v(-17.76, 271.38) * mm, "end": v(-47.76, 286.38) * mm});
            skLineSegment(sketch, "E211", {"start": v(47.76, 286.38) * mm, "end": v(17.76, 271.38) * mm});
            skArc(sketch, "E212", {"start": v(-47.76, 286.38) * mm, "mid": v(-52.63, 286.16) * mm, "end": v(-55, 281.9) * mm});
            skArc(sketch, "E213", {"start": v(55, 281.9) * mm, "mid": v(52.63, 286.16) * mm, "end": v(47.76, 286.38) * mm});
            skLineSegment(sketch, "E214", {"start": v(55, 220) * mm, "end": v(55, 281.9) * mm});
            skLineSegment(sketch, "E215", {"start": v(-55, 281.9) * mm, "end": v(-55, 220) * mm});
            skArc(sketch, "E216", {"start": v(88.23, 115.57) * mm, "mid": v(63.5, 165.2) * mm, "end": v(55, 220) * mm});
            skArc(sketch, "E217", {"start": v(-55, 220) * mm, "mid": v(-63.5, 165.2) * mm, "end": v(-88.23, 115.57) * mm});
            skArc(sketch, "E218", {"start": v(88.23, 115.57) * mm, "mid": v(122.8, 29.63) * mm, "end": v(114.93, -62.67) * mm});
            skArc(sketch, "E219", {"start": v(-114.93, -62.67) * mm, "mid": v(-122.8, 29.63) * mm, "end": v(-88.23, 115.57) * mm});
            skArc(sketch, "E220", {"start": v(114.93, -62.67) * mm, "mid": v(99.12, -107.04) * mm, "end": v(81.24, -150.61) * mm});
            skArc(sketch, "E221", {"start": v(-91.82, -125.55) * mm, "mid": v(-103.9, -94.3) * mm, "end": v(-114.93, -62.67) * mm});
            skLineSegment(sketch, "E222", {"start": v(15, 200) * mm, "end": v(15, 266.9) * mm});
            skLineSegment(sketch, "E223", {"start": v(-15, 266.9) * mm, "end": v(-15, 200) * mm});
            skFitSpline(sketch, "E224", {"points": [v(-91.82, -125.55) * mm, v(-91.62, -126.03) * mm, v(-91.26, -126.7) * mm, v(-90.63, -127.5) * mm, v(-90.08, -128.06) * mm, v(-89.48, -128.54) * mm, v(-88.82, -128.93) * mm, v(-88.1, -129.24) * mm, v(-87.6, -129.37) * mm, v(-87.34, -129.42) * mm]});
            skFitSpline(sketch, "E225", {"points": [v(75.78, -153.89) * mm, v(76.07, -153.92) * mm, v(76.5, -153.94) * mm, v(77.05, -153.88) * mm, v(77.48, -153.8) * mm, v(77.89, -153.69) * mm, v(78.29, -153.54) * mm, v(78.67, -153.37) * mm, v(79.05, -153.16) * mm, v(79.4, -152.92) * mm, v(79.73, -152.65) * mm, v(80.05, -152.37) * mm, v(80.44, -151.95) * mm, v(80.86, -151.37) * mm, v(81.12, -150.87) * mm, v(81.24, -150.61) * mm]});
            skEllipticalArc(sketch, "E226", {});
            skEllipticalArc(sketch, "E227", {});
            skFitSpline(sketch, "E228", {"points": [v(62.62, -145.37) * mm, v(62.45, -145.73) * mm, v(62.27, -146.3) * mm, v(62.14, -147.08) * mm, v(62.09, -147.88) * mm, v(62.16, -148.66) * mm, v(62.37, -149.44) * mm, v(62.6, -149.99) * mm, v(62.87, -150.5) * mm, v(63.22, -151) * mm, v(63.62, -151.44) * mm, v(64.07, -151.82) * mm, v(64.58, -152.15) * mm, v(65.12, -152.4) * mm, v(65.68, -152.6) * mm, v(66.08, -152.67) * mm, v(66.27, -152.7) * mm]});
            skFitSpline(sketch, "E229", {"points": [v(-76.66, -131.3) * mm, v(-76.43, -131.33) * mm, v(-75.98, -131.38) * mm, v(-75.4, -131.35) * mm, v(-74.94, -131.27) * mm, v(-74.5, -131.16) * mm, v(-73.96, -130.95) * mm, v(-73.36, -130.6) * mm, v(-72.83, -130.16) * mm, v(-72.37, -129.63) * mm, v(-72, -129.05) * mm, v(-71.71, -128.41) * mm, v(-71.5, -127.75) * mm, v(-71.38, -127.07) * mm, v(-71.34, -126.38) * mm, v(-71.37, -125.69) * mm, v(-71.5, -124.77) * mm, v(-71.7, -124.1) * mm, v(-71.87, -123.68) * mm]});
            skArc(sketch, "E230", {"start": v(44.38, 134.72) * mm, "mid": v(98.19, 49.04) * mm, "end": v(97.29, -52.12) * mm});
            skArc(sketch, "E231", {"start": v(-97.29, -52.12) * mm, "mid": v(-98.19, 49.04) * mm, "end": v(-44.38, 134.72) * mm});
            skArc(sketch, "E232", {"start": v(97.29, -52.12) * mm, "mid": v(81.4, -99.29) * mm, "end": v(62.62, -145.37) * mm});
            skArc(sketch, "E233", {"start": v(-71.87, -123.68) * mm, "mid": v(-85.43, -88.2) * mm, "end": v(-97.29, -52.12) * mm});
            skArc(sketch, "E234", {"start": v(44.38, 134.72) * mm, "mid": v(22.68, 164.2) * mm, "end": v(15, 200) * mm});
            skArc(sketch, "E235", {"start": v(-15, 200) * mm, "mid": v(-22.68, 164.2) * mm, "end": v(-44.38, 134.72) * mm});
            const initialGuessF24  = {"E226": [0.5581223579930771, 0.217305327537415, 1, 0, 1.2944271909999163, 0.4, 4.190347248712868, 4.199840950622759], "E227": [0.5581223579930771, 0.217305327537415, 1, 0, 1.2944271909999163, 0.4, 4.322621862564569, 4.330548029780888]};
            skSetInitialGuess(sketch, initialGuessF24);
            skSolve(sketch);
        }
        {
            var Q0;
            Q0 = qSketchRegion(id + "F24", true);
            extrude(context, id + "F25", {"entities" : qUnion([Q0]), "depth" : getVariable(context, 't'), "offsetDistance" : 25 * mm, "symmetric" : true});
        }
        {
            var Q0;
            Q0=qCreatedBy(makeId("Front.planeOp"),FACE);
            var Q1;
            Q1=sQuery(id+"F3.wireOp",EDGE,"E23");
            cPlane(context, id + "F26", {"entities" : qUnion([Q0, Q1]), "cplaneType" : CPlaneType.LINE_ANGLE, "offset" : 25 * mm, "angle" : 126 * degree, "width" : 150 * mm, "height" : 150 * mm});
        }
        {
            var Q0;
            Q0=qCreatedBy(id+"F26.planeOp",FACE);
            var sketch = newSketch(context, id + "F27", { "sketchPlane" : qUnion([Q0])});
            skLineSegment(sketch, "E236", {"start": v(88.23, 115.57) * mm, "end": v(88.23, 115.57) * mm});
            skLineSegment(sketch, "E237", {"start": v(-88.23, 115.57) * mm, "end": v(-88.23, 115.57) * mm});
            skLineSegment(sketch, "E238", {"start": v(44.38, 134.72) * mm, "end": v(44.38, 134.72) * mm});
            skLineSegment(sketch, "E239", {"start": v(-44.38, 134.72) * mm, "end": v(-44.38, 134.72) * mm});
            skArc(sketch, "E240", {"start": v(44.38, 134.72) * mm, "mid": v(22.68, 164.2) * mm, "end": v(15, 200) * mm});
            skArc(sketch, "E241", {"start": v(-15, 200) * mm, "mid": v(-22.68, 164.2) * mm, "end": v(-44.38, 134.72) * mm});
            skLineSegment(sketch, "E242", {"start": v(15, 200) * mm, "end": v(15, 266.9) * mm});
            skLineSegment(sketch, "E243", {"start": v(-15, 266.9) * mm, "end": v(-15, 200) * mm});
            skArc(sketch, "E244", {"start": v(44.38, 134.72) * mm, "mid": v(98.19, 49.04) * mm, "end": v(97.29, -52.12) * mm});
            skArc(sketch, "E245", {"start": v(-97.29, -52.12) * mm, "mid": v(-98.19, 49.04) * mm, "end": v(-44.38, 134.72) * mm});
            skArc(sketch, "E246", {"start": v(97.29, -52.12) * mm, "mid": v(80.14, -102.66) * mm, "end": v(59.66, -151.94) * mm});
            skArc(sketch, "E247", {"start": v(-78.01, -108.24) * mm, "mid": v(-88.17, -80.36) * mm, "end": v(-97.29, -52.12) * mm});
            skFitSpline(sketch, "E248", {"points": [v(59.66, -151.94) * mm, v(59.5, -152.28) * mm, v(59.32, -152.82) * mm, v(59.2, -153.56) * mm, v(59.15, -154.32) * mm, v(59.22, -155.07) * mm, v(59.42, -155.8) * mm, v(59.62, -156.33) * mm, v(59.89, -156.83) * mm, v(60.32, -157.47) * mm, v(60.84, -158) * mm, v(61.46, -158.45) * mm, v(61.96, -158.72) * mm, v(62.48, -158.93) * mm, v(62.85, -159.04) * mm, v(63.04, -159.08) * mm]});
            skFitSpline(sketch, "E249", {"points": [v(-83.71, -115.65) * mm, v(-83.48, -115.74) * mm, v(-83, -115.9) * mm, v(-82.38, -115.99) * mm, v(-81.87, -116) * mm, v(-81.37, -115.97) * mm, v(-80.88, -115.87) * mm, v(-80.4, -115.7) * mm, v(-80.06, -115.56) * mm, v(-79.73, -115.37) * mm, v(-79.42, -115.16) * mm, v(-79.13, -114.91) * mm, v(-78.86, -114.65) * mm, v(-78.62, -114.36) * mm, v(-78.32, -113.95) * mm, v(-78.08, -113.5) * mm, v(-77.89, -113.04) * mm, v(-77.73, -112.56) * mm, v(-77.59, -111.95) * mm, v(-77.5, -111.2) * mm, v(-77.51, -110.44) * mm, v(-77.6, -109.7) * mm, v(-77.76, -108.96) * mm, v(-77.92, -108.48) * mm, v(-78.01, -108.24) * mm]});
            skEllipticalArc(sketch, "E250", {});
            skEllipticalArc(sketch, "E251", {});
            skFitSpline(sketch, "E252", {"points": [v(-99.11, -107.05) * mm, v(-98.95, -107.48) * mm, v(-98.65, -108.09) * mm, v(-98.14, -108.84) * mm, v(-97.56, -109.55) * mm, v(-96.72, -110.3) * mm, v(-95.92, -110.76) * mm, v(-95.5, -110.94) * mm]});
            skFitSpline(sketch, "E253", {"points": [v(72.3, -160.99) * mm, v(72.59, -161.05) * mm, v(73.02, -161.1) * mm, v(73.6, -161.08) * mm, v(74.03, -161.03) * mm, v(74.46, -160.95) * mm, v(74.87, -160.83) * mm, v(75.27, -160.67) * mm, v(75.67, -160.48) * mm, v(76.04, -160.26) * mm, v(76.4, -160) * mm, v(76.72, -159.72) * mm, v(77.14, -159.31) * mm, v(77.58, -158.74) * mm, v(77.86, -158.24) * mm, v(77.98, -157.97) * mm]});
            skArc(sketch, "E254", {"start": v(88.23, 115.57) * mm, "mid": v(122.8, 29.63) * mm, "end": v(114.93, -62.67) * mm});
            skArc(sketch, "E255", {"start": v(-114.93, -62.67) * mm, "mid": v(-122.8, 29.63) * mm, "end": v(-88.23, 115.57) * mm});
            skArc(sketch, "E256", {"start": v(114.93, -62.67) * mm, "mid": v(97.67, -110.8) * mm, "end": v(77.98, -157.97) * mm});
            skArc(sketch, "E257", {"start": v(-99.11, -107.05) * mm, "mid": v(-107.28, -84.96) * mm, "end": v(-114.93, -62.67) * mm});
            skArc(sketch, "E258", {"start": v(88.23, 115.57) * mm, "mid": v(63.5, 165.2) * mm, "end": v(55, 220) * mm});
            skArc(sketch, "E259", {"start": v(-55, 220) * mm, "mid": v(-63.5, 165.2) * mm, "end": v(-88.23, 115.57) * mm});
            skLineSegment(sketch, "E260", {"start": v(55, 220) * mm, "end": v(55, 281.9) * mm});
            skLineSegment(sketch, "E261", {"start": v(-55, 281.9) * mm, "end": v(-55, 220) * mm});
            skArc(sketch, "E262", {"start": v(-47.76, 286.38) * mm, "mid": v(-52.63, 286.16) * mm, "end": v(-55, 281.9) * mm});
            skArc(sketch, "E263", {"start": v(55, 281.9) * mm, "mid": v(52.63, 286.16) * mm, "end": v(47.76, 286.38) * mm});
            skLineSegment(sketch, "E264", {"start": v(-17.76, 271.38) * mm, "end": v(-47.76, 286.38) * mm});
            skLineSegment(sketch, "E265", {"start": v(47.76, 286.38) * mm, "end": v(17.76, 271.38) * mm});
            skArc(sketch, "E266", {"start": v(-15, 266.9) * mm, "mid": v(-15.75, 269.54) * mm, "end": v(-17.76, 271.38) * mm});
            skArc(sketch, "E267", {"start": v(17.76, 271.38) * mm, "mid": v(15.75, 269.54) * mm, "end": v(15, 266.9) * mm});
            const initialGuessF27  = {"E250": [0.2934222879662536, 0.217305327537415, 1, 0, 0.6805206466816319, 0.4, 4.104062367155119, 4.125001707391018], "E251": [0.2934222879662536, 0.217305327537415, 1, 0, 0.6805206466816319, 0.4, 4.36702104933989, 4.381448441427692]};
            skSetInitialGuess(sketch, initialGuessF27);
            skSolve(sketch);
        }
        {
            var Q0;
            Q0 = qSketchRegion(id + "F27", true);
            extrude(context, id + "F28", {"entities" : qUnion([Q0]), "depth" : getVariable(context, 't'), "offsetDistance" : 25 * mm, "symmetric" : true});
        }
        {
            var Q0;
            Q0=qCreatedBy(makeId("Front.planeOp"),FACE);
            var Q1;
            Q1=sQuery(id+"F3.wireOp",EDGE,"E23");
            cPlane(context, id + "F29", {"entities" : qUnion([Q0, Q1]), "cplaneType" : CPlaneType.LINE_ANGLE, "offset" : 25 * mm, "angle" : 144 * degree, "width" : 150 * mm, "height" : 150 * mm});
        }
        {
            var Q0;
            Q0=qCreatedBy(id+"F29.planeOp",FACE);
            var sketch = newSketch(context, id + "F30", { "sketchPlane" : qUnion([Q0])});
            skArc(sketch, "E268", {"start": v(-15, 266.9) * mm, "mid": v(-15.75, 269.54) * mm, "end": v(-17.76, 271.38) * mm});
            skArc(sketch, "E269", {"start": v(17.76, 271.38) * mm, "mid": v(15.75, 269.54) * mm, "end": v(15, 266.9) * mm});
            skLineSegment(sketch, "E270", {"start": v(15, 200) * mm, "end": v(15, 266.9) * mm});
            skLineSegment(sketch, "E271", {"start": v(-15, 266.9) * mm, "end": v(-15, 200) * mm});
            skLineSegment(sketch, "E272", {"start": v(-17.76, 271.38) * mm, "end": v(-47.76, 286.38) * mm});
            skLineSegment(sketch, "E273", {"start": v(47.76, 286.38) * mm, "end": v(17.76, 271.38) * mm});
            skArc(sketch, "E274", {"start": v(-47.76, 286.38) * mm, "mid": v(-52.63, 286.16) * mm, "end": v(-55, 281.9) * mm});
            skArc(sketch, "E275", {"start": v(55, 281.9) * mm, "mid": v(52.63, 286.16) * mm, "end": v(47.76, 286.38) * mm});
            skLineSegment(sketch, "E276", {"start": v(55, 220) * mm, "end": v(55, 281.9) * mm});
            skLineSegment(sketch, "E277", {"start": v(-55, 281.9) * mm, "end": v(-55, 220) * mm});
            skArc(sketch, "E278", {"start": v(88.23, 115.57) * mm, "mid": v(63.5, 165.2) * mm, "end": v(55, 220) * mm});
            skArc(sketch, "E279", {"start": v(-55, 220) * mm, "mid": v(-63.5, 165.2) * mm, "end": v(-88.23, 115.57) * mm});
            skArc(sketch, "E280", {"start": v(88.23, 115.57) * mm, "mid": v(122.8, 29.63) * mm, "end": v(114.93, -62.67) * mm});
            skArc(sketch, "E281", {"start": v(-114.93, -62.67) * mm, "mid": v(-122.8, 29.63) * mm, "end": v(-88.23, 115.57) * mm});
            skArc(sketch, "E282", {"start": v(114.93, -62.67) * mm, "mid": v(96.73, -113.22) * mm, "end": v(75.84, -162.71) * mm});
            skArc(sketch, "E283", {"start": v(-106.95, -85.88) * mm, "mid": v(-111, -74.3) * mm, "end": v(-114.93, -62.67) * mm});
            skFitSpline(sketch, "E284", {"points": [v(-106.95, -85.88) * mm, v(-106.83, -86.23) * mm, v(-106.53, -86.89) * mm, v(-106.05, -87.65) * mm, v(-105.6, -88.21) * mm, v(-105.1, -88.74) * mm, v(-104.68, -89.08) * mm, v(-104.37, -89.28) * mm]});
            skFitSpline(sketch, "E285", {"points": [v(70.05, -165.57) * mm, v(70.34, -165.64) * mm, v(70.77, -165.7) * mm, v(71.35, -165.71) * mm, v(71.79, -165.68) * mm, v(72.22, -165.61) * mm, v(72.64, -165.5) * mm, v(73.06, -165.37) * mm, v(73.46, -165.19) * mm, v(73.84, -164.98) * mm, v(74.2, -164.74) * mm, v(74.55, -164.46) * mm, v(74.97, -164.06) * mm, v(75.43, -163.5) * mm, v(75.72, -162.98) * mm, v(75.84, -162.71) * mm]});
            skEllipticalArc(sketch, "E286", {});
            skEllipticalArc(sketch, "E287", {});
            skFitSpline(sketch, "E288", {"points": [v(57.69, -156.24) * mm, v(57.53, -156.58) * mm, v(57.35, -157.1) * mm, v(57.23, -157.82) * mm, v(57.2, -158.37) * mm, v(57.22, -158.92) * mm, v(57.3, -159.46) * mm, v(57.45, -160) * mm, v(57.65, -160.5) * mm, v(57.9, -161) * mm, v(58.31, -161.6) * mm, v(58.8, -162.14) * mm, v(59.4, -162.58) * mm, v(59.87, -162.86) * mm, v(60.37, -163.09) * mm, v(60.72, -163.2) * mm, v(60.9, -163.25) * mm]});
            skFitSpline(sketch, "E289", {"points": [v(-91.13, -97.95) * mm, v(-90.9, -98.1) * mm, v(-90.43, -98.35) * mm, v(-89.8, -98.58) * mm, v(-89.27, -98.7) * mm, v(-88.74, -98.77) * mm, v(-88.2, -98.78) * mm, v(-87.66, -98.7) * mm, v(-87.27, -98.61) * mm, v(-86.9, -98.49) * mm, v(-86.52, -98.32) * mm, v(-86.17, -98.12) * mm, v(-85.84, -97.89) * mm, v(-85.53, -97.63) * mm, v(-85.25, -97.33) * mm, v(-85, -97.02) * mm, v(-84.76, -96.69) * mm, v(-84.56, -96.34) * mm, v(-84.33, -95.84) * mm, v(-84.12, -95.2) * mm, v(-83.91, -94.14) * mm, v(-83.92, -93.06) * mm, v(-84.1, -92) * mm, v(-84.26, -91.48) * mm, v(-84.35, -91.22) * mm]});
            skArc(sketch, "E290", {"start": v(44.38, 134.72) * mm, "mid": v(98.19, 49.04) * mm, "end": v(97.29, -52.12) * mm});
            skArc(sketch, "E291", {"start": v(-97.29, -52.12) * mm, "mid": v(-98.19, 49.04) * mm, "end": v(-44.38, 134.72) * mm});
            skArc(sketch, "E292", {"start": v(44.38, 134.72) * mm, "mid": v(22.68, 164.2) * mm, "end": v(15, 200) * mm});
            skArc(sketch, "E293", {"start": v(-15, 200) * mm, "mid": v(-22.68, 164.2) * mm, "end": v(-44.38, 134.72) * mm});
            skArc(sketch, "E294", {"start": v(97.29, -52.12) * mm, "mid": v(79.3, -104.87) * mm, "end": v(57.69, -156.24) * mm});
            skArc(sketch, "E295", {"start": v(-84.35, -91.22) * mm, "mid": v(-91.07, -71.76) * mm, "end": v(-97.29, -52.12) * mm});
            const initialGuessF30  = {"E286": [0.21318377087211884, 0.217305327537415, 1, 0, 0.49442719099991594, 0.4, 4.0149274331954565, 4.0493782559911065], "E287": [0.21318377087211884, 0.217305327537415, 1, 0, 0.49442719099991594, 0.4, 4.399300177032452, 4.41869098053793]};
            skSetInitialGuess(sketch, initialGuessF30);
            skSolve(sketch);
        }
        {
            var Q0;
            Q0 = qSketchRegion(id + "F30", true);
            extrude(context, id + "F31", {"entities" : qUnion([Q0]), "depth" : getVariable(context, 't'), "offsetDistance" : 25 * mm, "symmetric" : true});
        }
        {
            var Q0;
            Q0=qCreatedBy(makeId("Front.planeOp"),FACE);
            var Q1;
            Q1=sQuery(id+"F3.wireOp",EDGE,"E23");
            cPlane(context, id + "F32", {"entities" : qUnion([Q0, Q1]), "cplaneType" : CPlaneType.LINE_ANGLE, "offset" : 25 * mm, "angle" : 162 * degree, "width" : 150 * mm, "height" : 150 * mm});
        }
        {
            var Q0;
            Q0=qCreatedBy(id+"F32.planeOp",FACE);
            var sketch = newSketch(context, id + "F33", { "sketchPlane" : qUnion([Q0])});
            skLineSegment(sketch, "E296", {"start": v(55, 220) * mm, "end": v(55, 281.9) * mm});
            skLineSegment(sketch, "E297", {"start": v(-55, 281.9) * mm, "end": v(-55, 220) * mm});
            skArc(sketch, "E298", {"start": v(88.23, 115.57) * mm, "mid": v(63.5, 165.2) * mm, "end": v(55, 220) * mm});
            skArc(sketch, "E299", {"start": v(-55, 220) * mm, "mid": v(-63.5, 165.2) * mm, "end": v(-88.23, 115.57) * mm});
            skArc(sketch, "E300", {"start": v(88.23, 115.57) * mm, "mid": v(122.8, 29.63) * mm, "end": v(114.93, -62.67) * mm});
            skArc(sketch, "E301", {"start": v(-114.93, -62.67) * mm, "mid": v(-122.8, 29.63) * mm, "end": v(-88.23, 115.57) * mm});
            skArc(sketch, "E302", {"start": v(114.93, -62.67) * mm, "mid": v(96.2, -114.56) * mm, "end": v(74.64, -165.34) * mm});
            skArc(sketch, "E303", {"start": v(-113.5, -66.95) * mm, "mid": v(-114.22, -64.81) * mm, "end": v(-114.93, -62.67) * mm});
            skFitSpline(sketch, "E304", {"points": [v(-113.5, -66.95) * mm, v(-113.35, -67.42) * mm, v(-113.03, -68.08) * mm, v(-112.44, -68.89) * mm, v(-112.1, -69.25) * mm, v(-111.92, -69.42) * mm]});
            skFitSpline(sketch, "E305", {"points": [v(68.8, -168.1) * mm, v(69.1, -168.19) * mm, v(69.52, -168.26) * mm, v(70.1, -168.28) * mm, v(70.55, -168.26) * mm, v(70.98, -168.2) * mm, v(71.4, -168.1) * mm, v(71.82, -167.97) * mm, v(72.23, -167.8) * mm, v(72.62, -167.6) * mm, v(72.99, -167.35) * mm, v(73.33, -167.08) * mm, v(73.77, -166.68) * mm, v(74.23, -166.12) * mm, v(74.52, -165.6) * mm, v(74.64, -165.34) * mm]});
            skEllipticalArc(sketch, "E306", {});
            skEllipticalArc(sketch, "E307", {});
            skFitSpline(sketch, "E308", {"points": [v(56.56, -158.66) * mm, v(56.4, -159) * mm, v(56.23, -159.5) * mm, v(56.11, -160.21) * mm, v(56.08, -160.76) * mm, v(56.1, -161.3) * mm, v(56.19, -161.83) * mm, v(56.33, -162.36) * mm, v(56.52, -162.86) * mm, v(56.77, -163.34) * mm, v(57.17, -163.95) * mm, v(57.66, -164.47) * mm, v(58.24, -164.92) * mm, v(58.85, -165.3) * mm, v(59.35, -165.5) * mm, v(59.7, -165.6) * mm]});
            skFitSpline(sketch, "E309", {"points": [v(-97.17, -82.42) * mm, v(-96.96, -82.6) * mm, v(-96.51, -82.92) * mm, v(-95.9, -83.23) * mm, v(-95.37, -83.42) * mm, v(-94.84, -83.57) * mm, v(-94.3, -83.65) * mm, v(-93.74, -83.65) * mm, v(-93.2, -83.61) * mm, v(-92.65, -83.5) * mm, v(-92.13, -83.3) * mm, v(-91.75, -83.13) * mm, v(-91.4, -82.93) * mm, v(-91.06, -82.69) * mm, v(-90.74, -82.42) * mm, v(-90.45, -82.12) * mm, v(-90.18, -81.8) * mm, v(-89.94, -81.46) * mm, v(-89.73, -81.1) * mm, v(-89.56, -80.73) * mm, v(-89.4, -80.35) * mm, v(-89.29, -79.95) * mm, v(-89.2, -79.54) * mm, v(-89.12, -79) * mm, v(-89.1, -78.44) * mm, v(-89.15, -77.89) * mm, v(-89.23, -77.34) * mm, v(-89.34, -76.94) * mm, v(-89.43, -76.68) * mm]});
            skArc(sketch, "E310", {"start": v(97.29, -52.12) * mm, "mid": v(78.83, -106.12) * mm, "end": v(56.56, -158.66) * mm});
            skArc(sketch, "E311", {"start": v(-89.43, -76.68) * mm, "mid": v(-93.46, -64.43) * mm, "end": v(-97.29, -52.12) * mm});
            skArc(sketch, "E312", {"start": v(44.38, 134.72) * mm, "mid": v(98.19, 49.04) * mm, "end": v(97.29, -52.12) * mm});
            skArc(sketch, "E313", {"start": v(-97.29, -52.12) * mm, "mid": v(-98.19, 49.04) * mm, "end": v(-44.38, 134.72) * mm});
            skArc(sketch, "E314", {"start": v(44.38, 134.72) * mm, "mid": v(22.68, 164.2) * mm, "end": v(15, 200) * mm});
            skArc(sketch, "E315", {"start": v(-15, 200) * mm, "mid": v(-22.68, 164.2) * mm, "end": v(-44.38, 134.72) * mm});
            skLineSegment(sketch, "E316", {"start": v(15, 200) * mm, "end": v(15, 266.9) * mm});
            skLineSegment(sketch, "E317", {"start": v(-15, 266.9) * mm, "end": v(-15, 200) * mm});
            skArc(sketch, "E318", {"start": v(-15, 266.9) * mm, "mid": v(-15.75, 269.54) * mm, "end": v(-17.76, 271.38) * mm});
            skArc(sketch, "E319", {"start": v(17.76, 271.38) * mm, "mid": v(15.75, 269.54) * mm, "end": v(15, 266.9) * mm});
            skLineSegment(sketch, "E320", {"start": v(-17.76, 271.38) * mm, "end": v(-47.76, 286.38) * mm});
            skLineSegment(sketch, "E321", {"start": v(47.76, 286.38) * mm, "end": v(17.76, 271.38) * mm});
            skArc(sketch, "E322", {"start": v(-47.76, 286.38) * mm, "mid": v(-52.63, 286.16) * mm, "end": v(-55, 281.9) * mm});
            skArc(sketch, "E323", {"start": v(55, 281.9) * mm, "mid": v(52.63, 286.16) * mm, "end": v(47.76, 286.38) * mm});
            const initialGuessF33  = {"E306": [0.18134494701990395, 0.217305327537415, 1, 0, 0.42058488969530694, 0.4, 3.9408111603901035, 3.988621643843478], "E307": [0.18134494701990395, 0.217305327537415, 1, 0, 0.42058488969530694, 0.4, 4.41896507814913, 4.44151568898267]};
            skSetInitialGuess(sketch, initialGuessF33);
            skSolve(sketch);
        }
        {
            var Q0;
            Q0 = qSketchRegion(id + "F33", true);
            extrude(context, id + "F34", {"entities" : qUnion([Q0]), "depth" : getVariable(context, 't'), "offsetDistance" : 25 * mm, "symmetric" : true});
        }
        {
            var Q0;
            Q0=qCreatedBy(makeId("Top.planeOp"),FACE);
            var sketch = newSketch(context, id + "F35", { "sketchPlane" : qUnion([Q0])});
            skCircle(sketch, "E324", {"center": v(0, 0) * mm, "radius": 95 * mm});
            skCircle(sketch, "E325", {"center": v(0, 0) * mm, "radius": 115 * mm});
            skCircle(sketch, "E326", {"center": v(0, 0) * mm, "radius": 105 * mm, "construction": true});
            skPoint(sketch, "E327", {"position": v(-105, -1.13) * mm});
            skSolve(sketch);
        }
        {
            var Q0;
            Q0 = qSketchRegion(id + "F35", true);
            extrude(context, id + "F36", {"entities" : qUnion([Q0]), "depth" : getVariable(context, 't'), "offsetDistance" : 25 * mm, "symmetric" : true});
        }
        {
            var Q0;
            Q0=qCreatedBy(makeId("Top.planeOp"),FACE);
            cPlane(context, id + "F37", {"entities" : qUnion([Q0]), "cplaneType" : CPlaneType.OFFSET, "offset" : 200 * mm, "width" : 150 * mm, "height" : 150 * mm});
        }
        {
            var Q0;
            Q0=qCreatedBy(id+"F37.planeOp",FACE);
            var sketch = newSketch(context, id + "F38", { "sketchPlane" : qUnion([Q0])});
            skCircle(sketch, "E328", {"center": v(0, 0) * mm, "radius": 25.04 * mm});
            skCircle(sketch, "E329", {"center": v(0, 0) * mm, "radius": 15.04 * mm, "construction": true});
            skPoint(sketch, "E330", {"position": v(-3.57, 14.61) * mm});
            skCircle(sketch, "E331", {"center": v(-11, 0) * mm, "radius": 1.5 * mm});
            skCircle(sketch, "E332", {"center": v(11, 0) * mm, "radius": 1.5 * mm});
            skLineSegment(sketch, "E333", {"start": v(-11, 0) * mm, "end": v(11, 0) * mm, "construction": true});
            skSolve(sketch);
        }
        {
            var Q0;
            Q0 = qSketchRegion(id + "F38", true);
            extrude(context, id + "F39", {"entities" : qUnion([Q0]), "depth" : getVariable(context, 't'), "offsetDistance" : 25 * mm, "symmetric" : true});
        }
        {
            var Q0;
            Q0=qCreatedBy(makeId("Top.planeOp"),FACE);
            cPlane(context, id + "F40", {"entities" : qUnion([Q0]), "cplaneType" : CPlaneType.OFFSET, "offset" : 146 * mm, "width" : 150 * mm, "height" : 150 * mm});
        }
        {
            var Q0;
            Q0=qCreatedBy(id+"F40.planeOp",FACE);
            var sketch = newSketch(context, id + "F41", { "sketchPlane" : qUnion([Q0])});
            skCircle(sketch, "E334", {"center": v(0, 0) * mm, "radius": 43.74 * mm});
            skCircle(sketch, "E335", {"center": v(0, 0) * mm, "radius": 26 * mm});
            skCircle(sketch, "E336", {"center": v(0, 0) * mm, "radius": 33.74 * mm, "construction": true});
            skPoint(sketch, "E337", {"position": v(9.35, -32.42) * mm});
            skSolve(sketch);
        }
        {
            var Q0;
            Q0=makeQuery(id+"F41.imprint","IMPRINT",FACE,{"disambiguationData":[TD([[makeQuery(id+"F41.imprint","IMPRINT",EDGE,{"derivedFrom":sQuery(id+"F41.wireOp",EDGE,"E334")}),1.0]])]});
            extrude(context, id + "F42", {"entities" : qUnion([Q0]), "depth" : getVariable(context, 't'), "offsetDistance" : 25 * mm, "symmetric" : true});
        }
        {
            var Q0;
            Q0=qCreatedBy(id+"F37.planeOp",FACE);
            cPlane(context, id + "F43", {"entities" : qUnion([Q0]), "cplaneType" : CPlaneType.OFFSET, "offset" : 50 * mm, "width" : 150 * mm, "height" : 150 * mm});
        }
        {
            var Q0;
            Q0=qCreatedBy(id+"F43.planeOp",FACE);
            var sketch = newSketch(context, id + "F44", { "sketchPlane" : qUnion([Q0])});
            skCircle(sketch, "E338", {"center": v(0, 0) * mm, "radius": 25.04 * mm});
            skCircle(sketch, "E339", {"center": v(0, 0) * mm, "radius": 15.04 * mm, "construction": true});
            skCircle(sketch, "E340", {"center": v(0, 0) * mm, "radius": 5.5 * mm});
            skPoint(sketch, "E341", {"position": v(-1.12, -15) * mm});
            skSolve(sketch);
        }
        {
            var Q0;
            Q0 = qSketchRegion(id + "F44", true);
            extrude(context, id + "F45", {"entities" : qUnion([Q0]), "depth" : getVariable(context, 't'), "offsetDistance" : 25 * mm, "symmetric" : true});
        }
        {
            var Q0;
            Q0=makeQuery(id+"F7.opExtrude","SWEPT_BODY",BODY,{"disambiguationData":[OSD([sQuery(id+"F6.wireOp",EDGE,"E56"),sQuery(id+"F6.wireOp",EDGE,"E57"),sQuery(id+"F6.wireOp",EDGE,"E58"),sQuery(id+"F6.wireOp",EDGE,"E59"),sQuery(id+"F6.wireOp",EDGE,"E60"),sQuery(id+"F6.wireOp",EDGE,"E61"),sQuery(id+"F6.wireOp",EDGE,"E62"),sQuery(id+"F6.wireOp",EDGE,"E63"),sQuery(id+"F6.wireOp",EDGE,"E64"),sQuery(id+"F6.wireOp",EDGE,"E65"),sQuery(id+"F6.wireOp",EDGE,"E66"),sQuery(id+"F6.wireOp",EDGE,"E67")])]});
            var Q1;
            Q1=sQuery(id+"F1.wireOp",EDGE,"E10");
            circularPattern(context, id + "F46", {"entities" : qUnion([Q0]), "axis" : qUnion([Q1]), "angle" : 360 * degree, "instanceCount" : 20, "equalSpace" : true, "computeTransformsWithoutBuiltin" : true});
        }
        {
            var Q0;
            Q0=qCreatedBy(makeId("Top.planeOp"),FACE);
            cPlane(context, id + "F47", {"entities" : qUnion([Q0]), "cplaneType" : CPlaneType.OFFSET, "offset" : 400 * mm, "width" : 150 * mm, "height" : 150 * mm});
        }
        {
            var Q0;
            Q0=qCreatedBy(id+"F47.planeOp",FACE);
            var sketch = newSketch(context, id + "F48", { "sketchPlane" : qUnion([Q0])});
            skCircle(sketch, "E342.0", {"center": v(0, 0) * mm, "radius": 5.5 * mm});
            skCircle(sketch, "E343", {"center": v(0, 0) * mm, "radius": 50 * mm});
            skCircle(sketch, "E344", {"center": v(4.85, 30.62) * mm, "radius": 2 * mm});
            skCircle(sketch, "E345", {"center": v(0, 0) * mm, "radius": 31 * mm, "construction": true});
            skLineSegment(sketch, "E346", {"start": v(0, 0) * mm, "end": v(4.85, 30.62) * mm, "construction": true});
            skCircle(sketch, "E347.1.0", {"center": v(-4.85, 30.62) * mm, "radius": 2 * mm});
            skCircle(sketch, "E347.2.0", {"center": v(-14.07, 27.62) * mm, "radius": 2 * mm});
            skCircle(sketch, "E347.3.0", {"center": v(-21.92, 21.92) * mm, "radius": 2 * mm});
            skCircle(sketch, "E347.4.0", {"center": v(-27.62, 14.07) * mm, "radius": 2 * mm});
            skCircle(sketch, "E347.5.0", {"center": v(-30.62, 4.85) * mm, "radius": 2 * mm});
            skCircle(sketch, "E347.6.0", {"center": v(-30.62, -4.85) * mm, "radius": 2 * mm});
            skCircle(sketch, "E347.7.0", {"center": v(-27.62, -14.07) * mm, "radius": 2 * mm});
            skCircle(sketch, "E347.8.0", {"center": v(-21.92, -21.92) * mm, "radius": 2 * mm});
            skCircle(sketch, "E347.9.0", {"center": v(-14.07, -27.62) * mm, "radius": 2 * mm});
            skCircle(sketch, "E347.10.0", {"center": v(-4.85, -30.62) * mm, "radius": 2 * mm});
            skCircle(sketch, "E347.11.0", {"center": v(4.85, -30.62) * mm, "radius": 2 * mm});
            skCircle(sketch, "E347.12.0", {"center": v(14.07, -27.62) * mm, "radius": 2 * mm});
            skCircle(sketch, "E347.13.0", {"center": v(21.92, -21.92) * mm, "radius": 2 * mm});
            skCircle(sketch, "E347.14.0", {"center": v(27.62, -14.07) * mm, "radius": 2 * mm});
            skCircle(sketch, "E347.15.0", {"center": v(30.62, -4.85) * mm, "radius": 2 * mm});
            skCircle(sketch, "E347.16.0", {"center": v(30.62, 4.85) * mm, "radius": 2 * mm});
            skCircle(sketch, "E347.17.0", {"center": v(27.62, 14.07) * mm, "radius": 2 * mm});
            skCircle(sketch, "E347.18.0", {"center": v(21.92, 21.92) * mm, "radius": 2 * mm});
            skCircle(sketch, "E347.19.0", {"center": v(14.07, 27.62) * mm, "radius": 2 * mm});
            skCircle(sketch, "E348", {"center": v(4.85, 30.62) * mm, "radius": 3.72 * mm, "construction": true});
            skSolve(sketch);
        }
        {
            var Q0;
            Q0=makeQuery(id+"F48.imprint","IMPRINT",FACE,{"disambiguationData":[TD([[makeQuery(id+"F48.imprint","IMPRINT",EDGE,{"derivedFrom":sQuery(id+"F48.wireOp",EDGE,"E342.0")}),-1.0]])]});
            extrude(context, id + "F49", {"entities" : qUnion([Q0]), "oppositeDirection" : true, "depth" : getVariable(context, 't'), "offsetDistance" : 25 * mm});
        }
        {
            var Q0;
            Q0=qCreatedBy(id+"F47.planeOp",FACE);
            cPlane(context, id + "F50", {"entities" : qUnion([Q0]), "cplaneType" : CPlaneType.OFFSET, "offset" : 20 * mm, "oppositeDirection" : true, "width" : 150 * mm, "height" : 150 * mm});
        }
        {
            var Q0;
            Q0=qCreatedBy(id+"F50.planeOp",FACE);
            var sketch = newSketch(context, id + "F51", { "sketchPlane" : qUnion([Q0])});
            skCircle(sketch, "E349.0", {"center": v(0, 0) * mm, "radius": 5.5 * mm});
            skCircle(sketch, "E350", {"center": v(0, 0) * mm, "radius": 25.04 * mm});
            skSolve(sketch);
        }
        {
            var Q0;
            Q0=makeQuery(id+"F51.imprint","IMPRINT",FACE,{"disambiguationData":[TD([[makeQuery(id+"F51.imprint","IMPRINT",EDGE,{"derivedFrom":sQuery(id+"F51.wireOp",EDGE,"E349.0")}),-1.0]])]});
            extrude(context, id + "F52", {"entities" : qUnion([Q0]), "depth" : getVariable(context, 't'), "offsetDistance" : 25 * mm, "symmetric" : true});
        }
        {
            var Q0;
            Q0=makeQuery(id+"F36.opExtrude","SWEPT_BODY",BODY,{"disambiguationData":[OSD([sQuery(id+"F35.wireOp",EDGE,"E324"),sQuery(id+"F35.wireOp",EDGE,"E325")])]});
            var Q1;
            Q1=makeQuery(id+"F39.opExtrude","SWEPT_BODY",BODY,{"disambiguationData":[OSD([sQuery(id+"F38.wireOp",EDGE,"E328"),sQuery(id+"F38.wireOp",EDGE,"or8u7yw1-5iI8-fih6-ifgH-aQ84WTj8Eifl")])]});
            var Q2;
            Q2=makeQuery(id+"F42.opExtrude","SWEPT_BODY",BODY,{"disambiguationData":[OSD([sQuery(id+"F41.wireOp",EDGE,"E334"),sQuery(id+"F41.wireOp",EDGE,"E335")])]});
            var Q3;
            Q3=makeQuery(id+"F45.opExtrude","SWEPT_BODY",BODY,{"disambiguationData":[OSD([sQuery(id+"F44.wireOp",EDGE,"E338"),sQuery(id+"F44.wireOp",EDGE,"E340")])]});
            var Q4;
            Q4=makeQuery(id+"F52.opExtrude","SWEPT_BODY",BODY,{"disambiguationData":[OSD([sQuery(id+"F51.wireOp",EDGE,"E349.0"),sQuery(id+"F51.wireOp",EDGE,"E350")])]});
            var Q5;
            Q5=makeQuery(id+"F7.opExtrude","SWEPT_BODY",BODY,{"disambiguationData":[OSD([sQuery(id+"F6.wireOp",EDGE,"E29"),sQuery(id+"F6.wireOp",EDGE,"E32"),sQuery(id+"F6.wireOp",EDGE,"E34"),sQuery(id+"F6.wireOp",EDGE,"E36"),sQuery(id+"F6.wireOp",EDGE,"E39"),sQuery(id+"F6.wireOp",EDGE,"E42"),sQuery(id+"F6.wireOp",EDGE,"E44"),sQuery(id+"F6.wireOp",EDGE,"E46"),sQuery(id+"F6.wireOp",EDGE,"E48"),sQuery(id+"F6.wireOp",EDGE,"E50"),sQuery(id+"F6.wireOp",EDGE,"E51"),sQuery(id+"F6.wireOp",EDGE,"E53"),sQuery(id+"F6.wireOp",EDGE,"E55")])]});
            var Q6;
            Q6=makeQuery(id+"F7.opExtrude","SWEPT_BODY",BODY,{"disambiguationData":[OSD([sQuery(id+"F6.wireOp",EDGE,"E30"),sQuery(id+"F6.wireOp",EDGE,"E31"),sQuery(id+"F6.wireOp",EDGE,"E33"),sQuery(id+"F6.wireOp",EDGE,"E35"),sQuery(id+"F6.wireOp",EDGE,"E37"),sQuery(id+"F6.wireOp",EDGE,"E38"),sQuery(id+"F6.wireOp",EDGE,"E40"),sQuery(id+"F6.wireOp",EDGE,"E41"),sQuery(id+"F6.wireOp",EDGE,"E43"),sQuery(id+"F6.wireOp",EDGE,"E45"),sQuery(id+"F6.wireOp",EDGE,"E47"),sQuery(id+"F6.wireOp",EDGE,"E49"),sQuery(id+"F6.wireOp",EDGE,"E52"),sQuery(id+"F6.wireOp",EDGE,"E54")])]});
            var Q7;
            Q7=makeQuery(id+"F10.opExtrude","SWEPT_BODY",BODY,{"disambiguationData":[OSD([sQuery(id+"F9.wireOp",EDGE,"E68"),sQuery(id+"F9.wireOp",EDGE,"E70"),sQuery(id+"F9.wireOp",EDGE,"E73"),sQuery(id+"F9.wireOp",EDGE,"E75"),sQuery(id+"F9.wireOp",EDGE,"E77"),sQuery(id+"F9.wireOp",EDGE,"E79"),sQuery(id+"F9.wireOp",EDGE,"E81"),sQuery(id+"F9.wireOp",EDGE,"E83"),sQuery(id+"F9.wireOp",EDGE,"E85"),sQuery(id+"F9.wireOp",EDGE,"E86"),sQuery(id+"F9.wireOp",EDGE,"E88"),sQuery(id+"F9.wireOp",EDGE,"E90"),sQuery(id+"F9.wireOp",EDGE,"E93"),sQuery(id+"F9.wireOp",EDGE,"E95")])]});
            var Q8;
            Q8=makeQuery(id+"F10.opExtrude","SWEPT_BODY",BODY,{"disambiguationData":[OSD([sQuery(id+"F9.wireOp",EDGE,"E69"),sQuery(id+"F9.wireOp",EDGE,"E71"),sQuery(id+"F9.wireOp",EDGE,"E72"),sQuery(id+"F9.wireOp",EDGE,"E74"),sQuery(id+"F9.wireOp",EDGE,"E76"),sQuery(id+"F9.wireOp",EDGE,"E78"),sQuery(id+"F9.wireOp",EDGE,"E80"),sQuery(id+"F9.wireOp",EDGE,"E82"),sQuery(id+"F9.wireOp",EDGE,"E84"),sQuery(id+"F9.wireOp",EDGE,"E87"),sQuery(id+"F9.wireOp",EDGE,"E89"),sQuery(id+"F9.wireOp",EDGE,"E91"),sQuery(id+"F9.wireOp",EDGE,"E92"),sQuery(id+"F9.wireOp",EDGE,"E94")])]});
            var Q9;
            Q9=makeQuery(id+"F13.opExtrude","SWEPT_BODY",BODY,{"disambiguationData":[OSD([sQuery(id+"F12.wireOp",EDGE,"E96"),sQuery(id+"F12.wireOp",EDGE,"E99"),sQuery(id+"F12.wireOp",EDGE,"E101"),sQuery(id+"F12.wireOp",EDGE,"E103"),sQuery(id+"F12.wireOp",EDGE,"E105"),sQuery(id+"F12.wireOp",EDGE,"E106"),sQuery(id+"F12.wireOp",EDGE,"E108"),sQuery(id+"F12.wireOp",EDGE,"E111"),sQuery(id+"F12.wireOp",EDGE,"E113"),sQuery(id+"F12.wireOp",EDGE,"E115"),sQuery(id+"F12.wireOp",EDGE,"E117"),sQuery(id+"F12.wireOp",EDGE,"E119"),sQuery(id+"F12.wireOp",EDGE,"E120"),sQuery(id+"F12.wireOp",EDGE,"E122")])]});
            var Q10;
            Q10=makeQuery(id+"F13.opExtrude","SWEPT_BODY",BODY,{"disambiguationData":[OSD([sQuery(id+"F12.wireOp",EDGE,"E97"),sQuery(id+"F12.wireOp",EDGE,"E98"),sQuery(id+"F12.wireOp",EDGE,"E100"),sQuery(id+"F12.wireOp",EDGE,"E102"),sQuery(id+"F12.wireOp",EDGE,"E104"),sQuery(id+"F12.wireOp",EDGE,"E107"),sQuery(id+"F12.wireOp",EDGE,"E109"),sQuery(id+"F12.wireOp",EDGE,"E110"),sQuery(id+"F12.wireOp",EDGE,"E112"),sQuery(id+"F12.wireOp",EDGE,"E114"),sQuery(id+"F12.wireOp",EDGE,"E116"),sQuery(id+"F12.wireOp",EDGE,"E118"),sQuery(id+"F12.wireOp",EDGE,"E121"),sQuery(id+"F12.wireOp",EDGE,"E123")])]});
            var Q11;
            Q11=makeQuery(id+"F16.opExtrude","SWEPT_BODY",BODY,{"disambiguationData":[OSD([sQuery(id+"F15.wireOp",EDGE,"E124"),sQuery(id+"F15.wireOp",EDGE,"E127"),sQuery(id+"F15.wireOp",EDGE,"E128"),sQuery(id+"F15.wireOp",EDGE,"E130"),sQuery(id+"F15.wireOp",EDGE,"E133"),sQuery(id+"F15.wireOp",EDGE,"E135"),sQuery(id+"F15.wireOp",EDGE,"E137"),sQuery(id+"F15.wireOp",EDGE,"E139"),sQuery(id+"F15.wireOp",EDGE,"E140"),sQuery(id+"F15.wireOp",EDGE,"E142"),sQuery(id+"F15.wireOp",EDGE,"E145"),sQuery(id+"F15.wireOp",EDGE,"E147"),sQuery(id+"F15.wireOp",EDGE,"E149"),sQuery(id+"F15.wireOp",EDGE,"E151")])]});
            var Q12;
            Q12=makeQuery(id+"F16.opExtrude","SWEPT_BODY",BODY,{"disambiguationData":[OSD([sQuery(id+"F15.wireOp",EDGE,"E125"),sQuery(id+"F15.wireOp",EDGE,"E126"),sQuery(id+"F15.wireOp",EDGE,"E129"),sQuery(id+"F15.wireOp",EDGE,"E131"),sQuery(id+"F15.wireOp",EDGE,"E132"),sQuery(id+"F15.wireOp",EDGE,"E134"),sQuery(id+"F15.wireOp",EDGE,"E136"),sQuery(id+"F15.wireOp",EDGE,"E138"),sQuery(id+"F15.wireOp",EDGE,"E141"),sQuery(id+"F15.wireOp",EDGE,"E143"),sQuery(id+"F15.wireOp",EDGE,"E144"),sQuery(id+"F15.wireOp",EDGE,"E146"),sQuery(id+"F15.wireOp",EDGE,"E148"),sQuery(id+"F15.wireOp",EDGE,"E150")])]});
            var Q13;
            Q13=makeQuery(id+"F19.opExtrude","SWEPT_BODY",BODY,{"disambiguationData":[OSD([sQuery(id+"F18.wireOp",EDGE,"E152"),sQuery(id+"F18.wireOp",EDGE,"E154"),sQuery(id+"F18.wireOp",EDGE,"E156"),sQuery(id+"F18.wireOp",EDGE,"E159"),sQuery(id+"F18.wireOp",EDGE,"E161"),sQuery(id+"F18.wireOp",EDGE,"E163"),sQuery(id+"F18.wireOp",EDGE,"E165"),sQuery(id+"F18.wireOp",EDGE,"E166"),sQuery(id+"F18.wireOp",EDGE,"E168"),sQuery(id+"F18.wireOp",EDGE,"E171"),sQuery(id+"F18.wireOp",EDGE,"E173"),sQuery(id+"F18.wireOp",EDGE,"E175"),sQuery(id+"F18.wireOp",EDGE,"E177"),sQuery(id+"F18.wireOp",EDGE,"E179")])]});
            var Q14;
            Q14=makeQuery(id+"F19.opExtrude","SWEPT_BODY",BODY,{"disambiguationData":[OSD([sQuery(id+"F18.wireOp",EDGE,"E153"),sQuery(id+"F18.wireOp",EDGE,"E155"),sQuery(id+"F18.wireOp",EDGE,"E157"),sQuery(id+"F18.wireOp",EDGE,"E158"),sQuery(id+"F18.wireOp",EDGE,"E160"),sQuery(id+"F18.wireOp",EDGE,"E162"),sQuery(id+"F18.wireOp",EDGE,"E164"),sQuery(id+"F18.wireOp",EDGE,"E167"),sQuery(id+"F18.wireOp",EDGE,"E169"),sQuery(id+"F18.wireOp",EDGE,"E170"),sQuery(id+"F18.wireOp",EDGE,"E172"),sQuery(id+"F18.wireOp",EDGE,"E174"),sQuery(id+"F18.wireOp",EDGE,"E176"),sQuery(id+"F18.wireOp",EDGE,"E178")])]});
            var Q15;
            Q15=makeQuery(id+"F22.opExtrude","SWEPT_BODY",BODY,{"disambiguationData":[OSD([sQuery(id+"F21.wireOp",EDGE,"E180"),sQuery(id+"F21.wireOp",EDGE,"E183"),sQuery(id+"F21.wireOp",EDGE,"E185"),sQuery(id+"F21.wireOp",EDGE,"E186"),sQuery(id+"F21.wireOp",EDGE,"E188"),sQuery(id+"F21.wireOp",EDGE,"E190"),sQuery(id+"F21.wireOp",EDGE,"E192"),sQuery(id+"F21.wireOp",EDGE,"E194"),sQuery(id+"F21.wireOp",EDGE,"E196"),sQuery(id+"F21.wireOp",EDGE,"E199"),sQuery(id+"F21.wireOp",EDGE,"E201"),sQuery(id+"F21.wireOp",EDGE,"E203"),sQuery(id+"F21.wireOp",EDGE,"E204"),sQuery(id+"F21.wireOp",EDGE,"E206")])]});
            var Q16;
            Q16=makeQuery(id+"F22.opExtrude","SWEPT_BODY",BODY,{"disambiguationData":[OSD([sQuery(id+"F21.wireOp",EDGE,"E181"),sQuery(id+"F21.wireOp",EDGE,"E182"),sQuery(id+"F21.wireOp",EDGE,"E184"),sQuery(id+"F21.wireOp",EDGE,"E187"),sQuery(id+"F21.wireOp",EDGE,"E189"),sQuery(id+"F21.wireOp",EDGE,"E191"),sQuery(id+"F21.wireOp",EDGE,"E193"),sQuery(id+"F21.wireOp",EDGE,"E195"),sQuery(id+"F21.wireOp",EDGE,"E197"),sQuery(id+"F21.wireOp",EDGE,"E198"),sQuery(id+"F21.wireOp",EDGE,"E200"),sQuery(id+"F21.wireOp",EDGE,"E202"),sQuery(id+"F21.wireOp",EDGE,"E205"),sQuery(id+"F21.wireOp",EDGE,"E207")])]});
            var Q17;
            Q17=makeQuery(id+"F25.opExtrude","SWEPT_BODY",BODY,{"disambiguationData":[OSD([sQuery(id+"F24.wireOp",EDGE,"E208"),sQuery(id+"F24.wireOp",EDGE,"E210"),sQuery(id+"F24.wireOp",EDGE,"E212"),sQuery(id+"F24.wireOp",EDGE,"E215"),sQuery(id+"F24.wireOp",EDGE,"E217"),sQuery(id+"F24.wireOp",EDGE,"E219"),sQuery(id+"F24.wireOp",EDGE,"E221"),sQuery(id+"F24.wireOp",EDGE,"E223"),sQuery(id+"F24.wireOp",EDGE,"E224"),sQuery(id+"F24.wireOp",EDGE,"E226"),sQuery(id+"F24.wireOp",EDGE,"E229"),sQuery(id+"F24.wireOp",EDGE,"E231"),sQuery(id+"F24.wireOp",EDGE,"E233"),sQuery(id+"F24.wireOp",EDGE,"E235")])]});
            var Q18;
            Q18=makeQuery(id+"F25.opExtrude","SWEPT_BODY",BODY,{"disambiguationData":[OSD([sQuery(id+"F24.wireOp",EDGE,"E209"),sQuery(id+"F24.wireOp",EDGE,"E211"),sQuery(id+"F24.wireOp",EDGE,"E213"),sQuery(id+"F24.wireOp",EDGE,"E214"),sQuery(id+"F24.wireOp",EDGE,"E216"),sQuery(id+"F24.wireOp",EDGE,"E218"),sQuery(id+"F24.wireOp",EDGE,"E220"),sQuery(id+"F24.wireOp",EDGE,"E222"),sQuery(id+"F24.wireOp",EDGE,"E225"),sQuery(id+"F24.wireOp",EDGE,"E227"),sQuery(id+"F24.wireOp",EDGE,"E228"),sQuery(id+"F24.wireOp",EDGE,"E230"),sQuery(id+"F24.wireOp",EDGE,"E232"),sQuery(id+"F24.wireOp",EDGE,"E234")])]});
            var Q19;
            Q19=makeQuery(id+"F28.opExtrude","SWEPT_BODY",BODY,{"disambiguationData":[OSD([sQuery(id+"F27.wireOp",EDGE,"E240"),sQuery(id+"F27.wireOp",EDGE,"E242"),sQuery(id+"F27.wireOp",EDGE,"E244"),sQuery(id+"F27.wireOp",EDGE,"E246"),sQuery(id+"F27.wireOp",EDGE,"E248"),sQuery(id+"F27.wireOp",EDGE,"E251"),sQuery(id+"F27.wireOp",EDGE,"E253"),sQuery(id+"F27.wireOp",EDGE,"E254"),sQuery(id+"F27.wireOp",EDGE,"E256"),sQuery(id+"F27.wireOp",EDGE,"E258"),sQuery(id+"F27.wireOp",EDGE,"E260"),sQuery(id+"F27.wireOp",EDGE,"E263"),sQuery(id+"F27.wireOp",EDGE,"E267"),sQuery(id+"F27.wireOp",EDGE,"E265")])]});
            var Q20;
            Q20=makeQuery(id+"F28.opExtrude","SWEPT_BODY",BODY,{"disambiguationData":[OSD([sQuery(id+"F27.wireOp",EDGE,"E241"),sQuery(id+"F27.wireOp",EDGE,"E243"),sQuery(id+"F27.wireOp",EDGE,"E245"),sQuery(id+"F27.wireOp",EDGE,"E247"),sQuery(id+"F27.wireOp",EDGE,"E249"),sQuery(id+"F27.wireOp",EDGE,"E250"),sQuery(id+"F27.wireOp",EDGE,"E252"),sQuery(id+"F27.wireOp",EDGE,"E255"),sQuery(id+"F27.wireOp",EDGE,"E257"),sQuery(id+"F27.wireOp",EDGE,"E259"),sQuery(id+"F27.wireOp",EDGE,"E261"),sQuery(id+"F27.wireOp",EDGE,"E262"),sQuery(id+"F27.wireOp",EDGE,"E266"),sQuery(id+"F27.wireOp",EDGE,"E264")])]});
            var Q21;
            Q21=makeQuery(id+"F31.opExtrude","SWEPT_BODY",BODY,{"disambiguationData":[OSD([sQuery(id+"F30.wireOp",EDGE,"E268"),sQuery(id+"F30.wireOp",EDGE,"E271"),sQuery(id+"F30.wireOp",EDGE,"E272"),sQuery(id+"F30.wireOp",EDGE,"E274"),sQuery(id+"F30.wireOp",EDGE,"E277"),sQuery(id+"F30.wireOp",EDGE,"E279"),sQuery(id+"F30.wireOp",EDGE,"E281"),sQuery(id+"F30.wireOp",EDGE,"E283"),sQuery(id+"F30.wireOp",EDGE,"E284"),sQuery(id+"F30.wireOp",EDGE,"E286"),sQuery(id+"F30.wireOp",EDGE,"E289"),sQuery(id+"F30.wireOp",EDGE,"E291"),sQuery(id+"F30.wireOp",EDGE,"E293"),sQuery(id+"F30.wireOp",EDGE,"E295")])]});
            var Q22;
            Q22=makeQuery(id+"F31.opExtrude","SWEPT_BODY",BODY,{"disambiguationData":[OSD([sQuery(id+"F30.wireOp",EDGE,"E269"),sQuery(id+"F30.wireOp",EDGE,"E270"),sQuery(id+"F30.wireOp",EDGE,"E273"),sQuery(id+"F30.wireOp",EDGE,"E275"),sQuery(id+"F30.wireOp",EDGE,"E276"),sQuery(id+"F30.wireOp",EDGE,"E278"),sQuery(id+"F30.wireOp",EDGE,"E280"),sQuery(id+"F30.wireOp",EDGE,"E282"),sQuery(id+"F30.wireOp",EDGE,"E285"),sQuery(id+"F30.wireOp",EDGE,"E287"),sQuery(id+"F30.wireOp",EDGE,"E288"),sQuery(id+"F30.wireOp",EDGE,"E290"),sQuery(id+"F30.wireOp",EDGE,"E292"),sQuery(id+"F30.wireOp",EDGE,"E294")])]});
            var Q23;
            Q23=makeQuery(id+"F34.opExtrude","SWEPT_BODY",BODY,{"disambiguationData":[OSD([sQuery(id+"F33.wireOp",EDGE,"E296"),sQuery(id+"F33.wireOp",EDGE,"E298"),sQuery(id+"F33.wireOp",EDGE,"E300"),sQuery(id+"F33.wireOp",EDGE,"E302"),sQuery(id+"F33.wireOp",EDGE,"E305"),sQuery(id+"F33.wireOp",EDGE,"E307"),sQuery(id+"F33.wireOp",EDGE,"E308"),sQuery(id+"F33.wireOp",EDGE,"E310"),sQuery(id+"F33.wireOp",EDGE,"E312"),sQuery(id+"F33.wireOp",EDGE,"E314"),sQuery(id+"F33.wireOp",EDGE,"E316"),sQuery(id+"F33.wireOp",EDGE,"E319"),sQuery(id+"F33.wireOp",EDGE,"E321"),sQuery(id+"F33.wireOp",EDGE,"E323")])]});
            var Q24;
            Q24=makeQuery(id+"F34.opExtrude","SWEPT_BODY",BODY,{"disambiguationData":[OSD([sQuery(id+"F33.wireOp",EDGE,"E297"),sQuery(id+"F33.wireOp",EDGE,"E299"),sQuery(id+"F33.wireOp",EDGE,"E301"),sQuery(id+"F33.wireOp",EDGE,"E303"),sQuery(id+"F33.wireOp",EDGE,"E304"),sQuery(id+"F33.wireOp",EDGE,"E306"),sQuery(id+"F33.wireOp",EDGE,"E309"),sQuery(id+"F33.wireOp",EDGE,"E311"),sQuery(id+"F33.wireOp",EDGE,"E313"),sQuery(id+"F33.wireOp",EDGE,"E315"),sQuery(id+"F33.wireOp",EDGE,"E317"),sQuery(id+"F33.wireOp",EDGE,"E318"),sQuery(id+"F33.wireOp",EDGE,"E320"),sQuery(id+"F33.wireOp",EDGE,"E322")])]});
            var Q25;
            Q25=makeQuery(id+"F46.opPattern","COPY",BODY,{"derivedFrom":makeQuery(id+"F7.opExtrude","SWEPT_BODY",BODY,{"disambiguationData":[OSD([sQuery(id+"F6.wireOp",EDGE,"E56"),sQuery(id+"F6.wireOp",EDGE,"E57"),sQuery(id+"F6.wireOp",EDGE,"E58"),sQuery(id+"F6.wireOp",EDGE,"E59"),sQuery(id+"F6.wireOp",EDGE,"E60"),sQuery(id+"F6.wireOp",EDGE,"E61"),sQuery(id+"F6.wireOp",EDGE,"E62"),sQuery(id+"F6.wireOp",EDGE,"E63"),sQuery(id+"F6.wireOp",EDGE,"E64"),sQuery(id+"F6.wireOp",EDGE,"E65"),sQuery(id+"F6.wireOp",EDGE,"E66"),sQuery(id+"F6.wireOp",EDGE,"E67")])]}),"instanceName":"1"});
            var Q26;
            Q26=makeQuery(id+"F46.opPattern","COPY",BODY,{"derivedFrom":makeQuery(id+"F7.opExtrude","SWEPT_BODY",BODY,{"disambiguationData":[OSD([sQuery(id+"F6.wireOp",EDGE,"E56"),sQuery(id+"F6.wireOp",EDGE,"E57"),sQuery(id+"F6.wireOp",EDGE,"E58"),sQuery(id+"F6.wireOp",EDGE,"E59"),sQuery(id+"F6.wireOp",EDGE,"E60"),sQuery(id+"F6.wireOp",EDGE,"E61"),sQuery(id+"F6.wireOp",EDGE,"E62"),sQuery(id+"F6.wireOp",EDGE,"E63"),sQuery(id+"F6.wireOp",EDGE,"E64"),sQuery(id+"F6.wireOp",EDGE,"E65"),sQuery(id+"F6.wireOp",EDGE,"E66"),sQuery(id+"F6.wireOp",EDGE,"E67")])]}),"instanceName":"2"});
            var Q27;
            Q27=makeQuery(id+"F46.opPattern","COPY",BODY,{"derivedFrom":makeQuery(id+"F7.opExtrude","SWEPT_BODY",BODY,{"disambiguationData":[OSD([sQuery(id+"F6.wireOp",EDGE,"E56"),sQuery(id+"F6.wireOp",EDGE,"E57"),sQuery(id+"F6.wireOp",EDGE,"E58"),sQuery(id+"F6.wireOp",EDGE,"E59"),sQuery(id+"F6.wireOp",EDGE,"E60"),sQuery(id+"F6.wireOp",EDGE,"E61"),sQuery(id+"F6.wireOp",EDGE,"E62"),sQuery(id+"F6.wireOp",EDGE,"E63"),sQuery(id+"F6.wireOp",EDGE,"E64"),sQuery(id+"F6.wireOp",EDGE,"E65"),sQuery(id+"F6.wireOp",EDGE,"E66"),sQuery(id+"F6.wireOp",EDGE,"E67")])]}),"instanceName":"3"});
            var Q28;
            Q28=makeQuery(id+"F46.opPattern","COPY",BODY,{"derivedFrom":makeQuery(id+"F7.opExtrude","SWEPT_BODY",BODY,{"disambiguationData":[OSD([sQuery(id+"F6.wireOp",EDGE,"E56"),sQuery(id+"F6.wireOp",EDGE,"E57"),sQuery(id+"F6.wireOp",EDGE,"E58"),sQuery(id+"F6.wireOp",EDGE,"E59"),sQuery(id+"F6.wireOp",EDGE,"E60"),sQuery(id+"F6.wireOp",EDGE,"E61"),sQuery(id+"F6.wireOp",EDGE,"E62"),sQuery(id+"F6.wireOp",EDGE,"E63"),sQuery(id+"F6.wireOp",EDGE,"E64"),sQuery(id+"F6.wireOp",EDGE,"E65"),sQuery(id+"F6.wireOp",EDGE,"E66"),sQuery(id+"F6.wireOp",EDGE,"E67")])]}),"instanceName":"4"});
            var Q29;
            Q29=makeQuery(id+"F46.opPattern","COPY",BODY,{"derivedFrom":makeQuery(id+"F7.opExtrude","SWEPT_BODY",BODY,{"disambiguationData":[OSD([sQuery(id+"F6.wireOp",EDGE,"E56"),sQuery(id+"F6.wireOp",EDGE,"E57"),sQuery(id+"F6.wireOp",EDGE,"E58"),sQuery(id+"F6.wireOp",EDGE,"E59"),sQuery(id+"F6.wireOp",EDGE,"E60"),sQuery(id+"F6.wireOp",EDGE,"E61"),sQuery(id+"F6.wireOp",EDGE,"E62"),sQuery(id+"F6.wireOp",EDGE,"E63"),sQuery(id+"F6.wireOp",EDGE,"E64"),sQuery(id+"F6.wireOp",EDGE,"E65"),sQuery(id+"F6.wireOp",EDGE,"E66"),sQuery(id+"F6.wireOp",EDGE,"E67")])]}),"instanceName":"5"});
            var Q30;
            Q30=makeQuery(id+"F46.opPattern","COPY",BODY,{"derivedFrom":makeQuery(id+"F7.opExtrude","SWEPT_BODY",BODY,{"disambiguationData":[OSD([sQuery(id+"F6.wireOp",EDGE,"E56"),sQuery(id+"F6.wireOp",EDGE,"E57"),sQuery(id+"F6.wireOp",EDGE,"E58"),sQuery(id+"F6.wireOp",EDGE,"E59"),sQuery(id+"F6.wireOp",EDGE,"E60"),sQuery(id+"F6.wireOp",EDGE,"E61"),sQuery(id+"F6.wireOp",EDGE,"E62"),sQuery(id+"F6.wireOp",EDGE,"E63"),sQuery(id+"F6.wireOp",EDGE,"E64"),sQuery(id+"F6.wireOp",EDGE,"E65"),sQuery(id+"F6.wireOp",EDGE,"E66"),sQuery(id+"F6.wireOp",EDGE,"E67")])]}),"instanceName":"6"});
            var Q31;
            Q31=makeQuery(id+"F46.opPattern","COPY",BODY,{"derivedFrom":makeQuery(id+"F7.opExtrude","SWEPT_BODY",BODY,{"disambiguationData":[OSD([sQuery(id+"F6.wireOp",EDGE,"E56"),sQuery(id+"F6.wireOp",EDGE,"E57"),sQuery(id+"F6.wireOp",EDGE,"E58"),sQuery(id+"F6.wireOp",EDGE,"E59"),sQuery(id+"F6.wireOp",EDGE,"E60"),sQuery(id+"F6.wireOp",EDGE,"E61"),sQuery(id+"F6.wireOp",EDGE,"E62"),sQuery(id+"F6.wireOp",EDGE,"E63"),sQuery(id+"F6.wireOp",EDGE,"E64"),sQuery(id+"F6.wireOp",EDGE,"E65"),sQuery(id+"F6.wireOp",EDGE,"E66"),sQuery(id+"F6.wireOp",EDGE,"E67")])]}),"instanceName":"7"});
            var Q32;
            Q32=makeQuery(id+"F46.opPattern","COPY",BODY,{"derivedFrom":makeQuery(id+"F7.opExtrude","SWEPT_BODY",BODY,{"disambiguationData":[OSD([sQuery(id+"F6.wireOp",EDGE,"E56"),sQuery(id+"F6.wireOp",EDGE,"E57"),sQuery(id+"F6.wireOp",EDGE,"E58"),sQuery(id+"F6.wireOp",EDGE,"E59"),sQuery(id+"F6.wireOp",EDGE,"E60"),sQuery(id+"F6.wireOp",EDGE,"E61"),sQuery(id+"F6.wireOp",EDGE,"E62"),sQuery(id+"F6.wireOp",EDGE,"E63"),sQuery(id+"F6.wireOp",EDGE,"E64"),sQuery(id+"F6.wireOp",EDGE,"E65"),sQuery(id+"F6.wireOp",EDGE,"E66"),sQuery(id+"F6.wireOp",EDGE,"E67")])]}),"instanceName":"8"});
            var Q33;
            Q33=makeQuery(id+"F46.opPattern","COPY",BODY,{"derivedFrom":makeQuery(id+"F7.opExtrude","SWEPT_BODY",BODY,{"disambiguationData":[OSD([sQuery(id+"F6.wireOp",EDGE,"E56"),sQuery(id+"F6.wireOp",EDGE,"E57"),sQuery(id+"F6.wireOp",EDGE,"E58"),sQuery(id+"F6.wireOp",EDGE,"E59"),sQuery(id+"F6.wireOp",EDGE,"E60"),sQuery(id+"F6.wireOp",EDGE,"E61"),sQuery(id+"F6.wireOp",EDGE,"E62"),sQuery(id+"F6.wireOp",EDGE,"E63"),sQuery(id+"F6.wireOp",EDGE,"E64"),sQuery(id+"F6.wireOp",EDGE,"E65"),sQuery(id+"F6.wireOp",EDGE,"E66"),sQuery(id+"F6.wireOp",EDGE,"E67")])]}),"instanceName":"9"});
            var Q34;
            Q34=makeQuery(id+"F46.opPattern","COPY",BODY,{"derivedFrom":makeQuery(id+"F7.opExtrude","SWEPT_BODY",BODY,{"disambiguationData":[OSD([sQuery(id+"F6.wireOp",EDGE,"E56"),sQuery(id+"F6.wireOp",EDGE,"E57"),sQuery(id+"F6.wireOp",EDGE,"E58"),sQuery(id+"F6.wireOp",EDGE,"E59"),sQuery(id+"F6.wireOp",EDGE,"E60"),sQuery(id+"F6.wireOp",EDGE,"E61"),sQuery(id+"F6.wireOp",EDGE,"E62"),sQuery(id+"F6.wireOp",EDGE,"E63"),sQuery(id+"F6.wireOp",EDGE,"E64"),sQuery(id+"F6.wireOp",EDGE,"E65"),sQuery(id+"F6.wireOp",EDGE,"E66"),sQuery(id+"F6.wireOp",EDGE,"E67")])]}),"instanceName":"10"});
            var Q35;
            Q35=makeQuery(id+"F46.opPattern","COPY",BODY,{"derivedFrom":makeQuery(id+"F7.opExtrude","SWEPT_BODY",BODY,{"disambiguationData":[OSD([sQuery(id+"F6.wireOp",EDGE,"E56"),sQuery(id+"F6.wireOp",EDGE,"E57"),sQuery(id+"F6.wireOp",EDGE,"E58"),sQuery(id+"F6.wireOp",EDGE,"E59"),sQuery(id+"F6.wireOp",EDGE,"E60"),sQuery(id+"F6.wireOp",EDGE,"E61"),sQuery(id+"F6.wireOp",EDGE,"E62"),sQuery(id+"F6.wireOp",EDGE,"E63"),sQuery(id+"F6.wireOp",EDGE,"E64"),sQuery(id+"F6.wireOp",EDGE,"E65"),sQuery(id+"F6.wireOp",EDGE,"E66"),sQuery(id+"F6.wireOp",EDGE,"E67")])]}),"instanceName":"11"});
            var Q36;
            Q36=makeQuery(id+"F46.opPattern","COPY",BODY,{"derivedFrom":makeQuery(id+"F7.opExtrude","SWEPT_BODY",BODY,{"disambiguationData":[OSD([sQuery(id+"F6.wireOp",EDGE,"E56"),sQuery(id+"F6.wireOp",EDGE,"E57"),sQuery(id+"F6.wireOp",EDGE,"E58"),sQuery(id+"F6.wireOp",EDGE,"E59"),sQuery(id+"F6.wireOp",EDGE,"E60"),sQuery(id+"F6.wireOp",EDGE,"E61"),sQuery(id+"F6.wireOp",EDGE,"E62"),sQuery(id+"F6.wireOp",EDGE,"E63"),sQuery(id+"F6.wireOp",EDGE,"E64"),sQuery(id+"F6.wireOp",EDGE,"E65"),sQuery(id+"F6.wireOp",EDGE,"E66"),sQuery(id+"F6.wireOp",EDGE,"E67")])]}),"instanceName":"12"});
            var Q37;
            Q37=makeQuery(id+"F46.opPattern","COPY",BODY,{"derivedFrom":makeQuery(id+"F7.opExtrude","SWEPT_BODY",BODY,{"disambiguationData":[OSD([sQuery(id+"F6.wireOp",EDGE,"E56"),sQuery(id+"F6.wireOp",EDGE,"E57"),sQuery(id+"F6.wireOp",EDGE,"E58"),sQuery(id+"F6.wireOp",EDGE,"E59"),sQuery(id+"F6.wireOp",EDGE,"E60"),sQuery(id+"F6.wireOp",EDGE,"E61"),sQuery(id+"F6.wireOp",EDGE,"E62"),sQuery(id+"F6.wireOp",EDGE,"E63"),sQuery(id+"F6.wireOp",EDGE,"E64"),sQuery(id+"F6.wireOp",EDGE,"E65"),sQuery(id+"F6.wireOp",EDGE,"E66"),sQuery(id+"F6.wireOp",EDGE,"E67")])]}),"instanceName":"13"});
            var Q38;
            Q38=makeQuery(id+"F46.opPattern","COPY",BODY,{"derivedFrom":makeQuery(id+"F7.opExtrude","SWEPT_BODY",BODY,{"disambiguationData":[OSD([sQuery(id+"F6.wireOp",EDGE,"E56"),sQuery(id+"F6.wireOp",EDGE,"E57"),sQuery(id+"F6.wireOp",EDGE,"E58"),sQuery(id+"F6.wireOp",EDGE,"E59"),sQuery(id+"F6.wireOp",EDGE,"E60"),sQuery(id+"F6.wireOp",EDGE,"E61"),sQuery(id+"F6.wireOp",EDGE,"E62"),sQuery(id+"F6.wireOp",EDGE,"E63"),sQuery(id+"F6.wireOp",EDGE,"E64"),sQuery(id+"F6.wireOp",EDGE,"E65"),sQuery(id+"F6.wireOp",EDGE,"E66"),sQuery(id+"F6.wireOp",EDGE,"E67")])]}),"instanceName":"14"});
            var Q39;
            Q39=makeQuery(id+"F46.opPattern","COPY",BODY,{"derivedFrom":makeQuery(id+"F7.opExtrude","SWEPT_BODY",BODY,{"disambiguationData":[OSD([sQuery(id+"F6.wireOp",EDGE,"E56"),sQuery(id+"F6.wireOp",EDGE,"E57"),sQuery(id+"F6.wireOp",EDGE,"E58"),sQuery(id+"F6.wireOp",EDGE,"E59"),sQuery(id+"F6.wireOp",EDGE,"E60"),sQuery(id+"F6.wireOp",EDGE,"E61"),sQuery(id+"F6.wireOp",EDGE,"E62"),sQuery(id+"F6.wireOp",EDGE,"E63"),sQuery(id+"F6.wireOp",EDGE,"E64"),sQuery(id+"F6.wireOp",EDGE,"E65"),sQuery(id+"F6.wireOp",EDGE,"E66"),sQuery(id+"F6.wireOp",EDGE,"E67")])]}),"instanceName":"15"});
            var Q40;
            Q40=makeQuery(id+"F46.opPattern","COPY",BODY,{"derivedFrom":makeQuery(id+"F7.opExtrude","SWEPT_BODY",BODY,{"disambiguationData":[OSD([sQuery(id+"F6.wireOp",EDGE,"E56"),sQuery(id+"F6.wireOp",EDGE,"E57"),sQuery(id+"F6.wireOp",EDGE,"E58"),sQuery(id+"F6.wireOp",EDGE,"E59"),sQuery(id+"F6.wireOp",EDGE,"E60"),sQuery(id+"F6.wireOp",EDGE,"E61"),sQuery(id+"F6.wireOp",EDGE,"E62"),sQuery(id+"F6.wireOp",EDGE,"E63"),sQuery(id+"F6.wireOp",EDGE,"E64"),sQuery(id+"F6.wireOp",EDGE,"E65"),sQuery(id+"F6.wireOp",EDGE,"E66"),sQuery(id+"F6.wireOp",EDGE,"E67")])]}),"instanceName":"16"});
            var Q41;
            Q41=makeQuery(id+"F46.opPattern","COPY",BODY,{"derivedFrom":makeQuery(id+"F7.opExtrude","SWEPT_BODY",BODY,{"disambiguationData":[OSD([sQuery(id+"F6.wireOp",EDGE,"E56"),sQuery(id+"F6.wireOp",EDGE,"E57"),sQuery(id+"F6.wireOp",EDGE,"E58"),sQuery(id+"F6.wireOp",EDGE,"E59"),sQuery(id+"F6.wireOp",EDGE,"E60"),sQuery(id+"F6.wireOp",EDGE,"E61"),sQuery(id+"F6.wireOp",EDGE,"E62"),sQuery(id+"F6.wireOp",EDGE,"E63"),sQuery(id+"F6.wireOp",EDGE,"E64"),sQuery(id+"F6.wireOp",EDGE,"E65"),sQuery(id+"F6.wireOp",EDGE,"E66"),sQuery(id+"F6.wireOp",EDGE,"E67")])]}),"instanceName":"17"});
            var Q42;
            Q42=makeQuery(id+"F46.opPattern","COPY",BODY,{"derivedFrom":makeQuery(id+"F7.opExtrude","SWEPT_BODY",BODY,{"disambiguationData":[OSD([sQuery(id+"F6.wireOp",EDGE,"E56"),sQuery(id+"F6.wireOp",EDGE,"E57"),sQuery(id+"F6.wireOp",EDGE,"E58"),sQuery(id+"F6.wireOp",EDGE,"E59"),sQuery(id+"F6.wireOp",EDGE,"E60"),sQuery(id+"F6.wireOp",EDGE,"E61"),sQuery(id+"F6.wireOp",EDGE,"E62"),sQuery(id+"F6.wireOp",EDGE,"E63"),sQuery(id+"F6.wireOp",EDGE,"E64"),sQuery(id+"F6.wireOp",EDGE,"E65"),sQuery(id+"F6.wireOp",EDGE,"E66"),sQuery(id+"F6.wireOp",EDGE,"E67")])]}),"instanceName":"18"});
            var Q43;
            Q43=makeQuery(id+"F46.opPattern","COPY",BODY,{"derivedFrom":makeQuery(id+"F7.opExtrude","SWEPT_BODY",BODY,{"disambiguationData":[OSD([sQuery(id+"F6.wireOp",EDGE,"E56"),sQuery(id+"F6.wireOp",EDGE,"E57"),sQuery(id+"F6.wireOp",EDGE,"E58"),sQuery(id+"F6.wireOp",EDGE,"E59"),sQuery(id+"F6.wireOp",EDGE,"E60"),sQuery(id+"F6.wireOp",EDGE,"E61"),sQuery(id+"F6.wireOp",EDGE,"E62"),sQuery(id+"F6.wireOp",EDGE,"E63"),sQuery(id+"F6.wireOp",EDGE,"E64"),sQuery(id+"F6.wireOp",EDGE,"E65"),sQuery(id+"F6.wireOp",EDGE,"E66"),sQuery(id+"F6.wireOp",EDGE,"E67")])]}),"instanceName":"19"});
            var Q44;
            Q44=makeQuery(id+"F7.opExtrude","SWEPT_BODY",BODY,{"disambiguationData":[OSD([sQuery(id+"F6.wireOp",EDGE,"E56"),sQuery(id+"F6.wireOp",EDGE,"E57"),sQuery(id+"F6.wireOp",EDGE,"E58"),sQuery(id+"F6.wireOp",EDGE,"E59"),sQuery(id+"F6.wireOp",EDGE,"E60"),sQuery(id+"F6.wireOp",EDGE,"E61"),sQuery(id+"F6.wireOp",EDGE,"E62"),sQuery(id+"F6.wireOp",EDGE,"E63"),sQuery(id+"F6.wireOp",EDGE,"E64"),sQuery(id+"F6.wireOp",EDGE,"E65"),sQuery(id+"F6.wireOp",EDGE,"E66"),sQuery(id+"F6.wireOp",EDGE,"E67")])]});
            var Q45;
            Q45=makeQuery(id+"F36.opExtrude","SWEPT_FACE",FACE,{"disambiguationData":[OSD([sQuery(id+"F35.wireOp",EDGE,"E325")])]});
            var Q46;
            Q46=makeQuery(id+"F39.opExtrude","SWEPT_FACE",FACE,{"disambiguationData":[OSD([sQuery(id+"F38.wireOp",EDGE,"E328")])]});
            var Q47;
            Q47=makeQuery(id+"F42.opExtrude","SWEPT_FACE",FACE,{"disambiguationData":[OSD([sQuery(id+"F41.wireOp",EDGE,"E334")])]});
            var Q48;
            Q48=makeQuery(id+"F45.opExtrude","SWEPT_FACE",FACE,{"disambiguationData":[OSD([sQuery(id+"F44.wireOp",EDGE,"E338")])]});
            var Q49;
            Q49=makeQuery(id+"F52.opExtrude","SWEPT_FACE",FACE,{"disambiguationData":[OSD([sQuery(id+"F51.wireOp",EDGE,"E350")])]});
            booleanBodies(context, id + "F53", {"operationType" : BooleanOperationType.SUBTRACTION, "tools" : qUnion([Q0, Q1, Q2, Q3, Q4]), "targets" : qUnion([Q5, Q6, Q7, Q8, Q9, Q10, Q11, Q12, Q13, Q14, Q15, Q16, Q17, Q18, Q19, Q20, Q21, Q22, Q23, Q24, Q25, Q26, Q27, Q28, Q29, Q30, Q31, Q32, Q33, Q34, Q35, Q36, Q37, Q38, Q39, Q40, Q41, Q42, Q43, Q44]), "offset" : true, "entitiesToOffset" : qUnion([Q45, Q46, Q47, Q48, Q49]), "offsetDistance" : 5 * mm, "oppositeDirection" : true, "keepTools" : true});
        }
        {
            var Q0;
            Q0=makeQuery(id+"F7.opExtrude","SWEPT_BODY",BODY,{"disambiguationData":[OSD([sQuery(id+"F6.wireOp",EDGE,"E29"),sQuery(id+"F6.wireOp",EDGE,"E32"),sQuery(id+"F6.wireOp",EDGE,"E34"),sQuery(id+"F6.wireOp",EDGE,"E36"),sQuery(id+"F6.wireOp",EDGE,"E39"),sQuery(id+"F6.wireOp",EDGE,"E42"),sQuery(id+"F6.wireOp",EDGE,"E44"),sQuery(id+"F6.wireOp",EDGE,"E46"),sQuery(id+"F6.wireOp",EDGE,"E48"),sQuery(id+"F6.wireOp",EDGE,"E50"),sQuery(id+"F6.wireOp",EDGE,"E51"),sQuery(id+"F6.wireOp",EDGE,"E53"),sQuery(id+"F6.wireOp",EDGE,"E55")])]});
            var Q1;
            Q1=makeQuery(id+"F7.opExtrude","SWEPT_BODY",BODY,{"disambiguationData":[OSD([sQuery(id+"F6.wireOp",EDGE,"E30"),sQuery(id+"F6.wireOp",EDGE,"E31"),sQuery(id+"F6.wireOp",EDGE,"E33"),sQuery(id+"F6.wireOp",EDGE,"E35"),sQuery(id+"F6.wireOp",EDGE,"E37"),sQuery(id+"F6.wireOp",EDGE,"E38"),sQuery(id+"F6.wireOp",EDGE,"E40"),sQuery(id+"F6.wireOp",EDGE,"E41"),sQuery(id+"F6.wireOp",EDGE,"E43"),sQuery(id+"F6.wireOp",EDGE,"E45"),sQuery(id+"F6.wireOp",EDGE,"E47"),sQuery(id+"F6.wireOp",EDGE,"E49"),sQuery(id+"F6.wireOp",EDGE,"E52"),sQuery(id+"F6.wireOp",EDGE,"E54")])]});
            var Q2;
            Q2=makeQuery(id+"F10.opExtrude","SWEPT_BODY",BODY,{"disambiguationData":[OSD([sQuery(id+"F9.wireOp",EDGE,"E68"),sQuery(id+"F9.wireOp",EDGE,"E70"),sQuery(id+"F9.wireOp",EDGE,"E73"),sQuery(id+"F9.wireOp",EDGE,"E75"),sQuery(id+"F9.wireOp",EDGE,"E77"),sQuery(id+"F9.wireOp",EDGE,"E79"),sQuery(id+"F9.wireOp",EDGE,"E81"),sQuery(id+"F9.wireOp",EDGE,"E83"),sQuery(id+"F9.wireOp",EDGE,"E85"),sQuery(id+"F9.wireOp",EDGE,"E86"),sQuery(id+"F9.wireOp",EDGE,"E88"),sQuery(id+"F9.wireOp",EDGE,"E90"),sQuery(id+"F9.wireOp",EDGE,"E93"),sQuery(id+"F9.wireOp",EDGE,"E95")])]});
            var Q3;
            Q3=makeQuery(id+"F10.opExtrude","SWEPT_BODY",BODY,{"disambiguationData":[OSD([sQuery(id+"F9.wireOp",EDGE,"E69"),sQuery(id+"F9.wireOp",EDGE,"E71"),sQuery(id+"F9.wireOp",EDGE,"E72"),sQuery(id+"F9.wireOp",EDGE,"E74"),sQuery(id+"F9.wireOp",EDGE,"E76"),sQuery(id+"F9.wireOp",EDGE,"E78"),sQuery(id+"F9.wireOp",EDGE,"E80"),sQuery(id+"F9.wireOp",EDGE,"E82"),sQuery(id+"F9.wireOp",EDGE,"E84"),sQuery(id+"F9.wireOp",EDGE,"E87"),sQuery(id+"F9.wireOp",EDGE,"E89"),sQuery(id+"F9.wireOp",EDGE,"E91"),sQuery(id+"F9.wireOp",EDGE,"E92"),sQuery(id+"F9.wireOp",EDGE,"E94")])]});
            var Q4;
            Q4=makeQuery(id+"F13.opExtrude","SWEPT_BODY",BODY,{"disambiguationData":[OSD([sQuery(id+"F12.wireOp",EDGE,"E96"),sQuery(id+"F12.wireOp",EDGE,"E99"),sQuery(id+"F12.wireOp",EDGE,"E101"),sQuery(id+"F12.wireOp",EDGE,"E103"),sQuery(id+"F12.wireOp",EDGE,"E105"),sQuery(id+"F12.wireOp",EDGE,"E106"),sQuery(id+"F12.wireOp",EDGE,"E108"),sQuery(id+"F12.wireOp",EDGE,"E111"),sQuery(id+"F12.wireOp",EDGE,"E113"),sQuery(id+"F12.wireOp",EDGE,"E115"),sQuery(id+"F12.wireOp",EDGE,"E117"),sQuery(id+"F12.wireOp",EDGE,"E119"),sQuery(id+"F12.wireOp",EDGE,"E120"),sQuery(id+"F12.wireOp",EDGE,"E122")])]});
            var Q5;
            Q5=makeQuery(id+"F13.opExtrude","SWEPT_BODY",BODY,{"disambiguationData":[OSD([sQuery(id+"F12.wireOp",EDGE,"E97"),sQuery(id+"F12.wireOp",EDGE,"E98"),sQuery(id+"F12.wireOp",EDGE,"E100"),sQuery(id+"F12.wireOp",EDGE,"E102"),sQuery(id+"F12.wireOp",EDGE,"E104"),sQuery(id+"F12.wireOp",EDGE,"E107"),sQuery(id+"F12.wireOp",EDGE,"E109"),sQuery(id+"F12.wireOp",EDGE,"E110"),sQuery(id+"F12.wireOp",EDGE,"E112"),sQuery(id+"F12.wireOp",EDGE,"E114"),sQuery(id+"F12.wireOp",EDGE,"E116"),sQuery(id+"F12.wireOp",EDGE,"E118"),sQuery(id+"F12.wireOp",EDGE,"E121"),sQuery(id+"F12.wireOp",EDGE,"E123")])]});
            var Q6;
            Q6=makeQuery(id+"F16.opExtrude","SWEPT_BODY",BODY,{"disambiguationData":[OSD([sQuery(id+"F15.wireOp",EDGE,"E124"),sQuery(id+"F15.wireOp",EDGE,"E127"),sQuery(id+"F15.wireOp",EDGE,"E128"),sQuery(id+"F15.wireOp",EDGE,"E130"),sQuery(id+"F15.wireOp",EDGE,"E133"),sQuery(id+"F15.wireOp",EDGE,"E135"),sQuery(id+"F15.wireOp",EDGE,"E137"),sQuery(id+"F15.wireOp",EDGE,"E139"),sQuery(id+"F15.wireOp",EDGE,"E140"),sQuery(id+"F15.wireOp",EDGE,"E142"),sQuery(id+"F15.wireOp",EDGE,"E145"),sQuery(id+"F15.wireOp",EDGE,"E147"),sQuery(id+"F15.wireOp",EDGE,"E149"),sQuery(id+"F15.wireOp",EDGE,"E151")])]});
            var Q7;
            Q7=makeQuery(id+"F16.opExtrude","SWEPT_BODY",BODY,{"disambiguationData":[OSD([sQuery(id+"F15.wireOp",EDGE,"E125"),sQuery(id+"F15.wireOp",EDGE,"E126"),sQuery(id+"F15.wireOp",EDGE,"E129"),sQuery(id+"F15.wireOp",EDGE,"E131"),sQuery(id+"F15.wireOp",EDGE,"E132"),sQuery(id+"F15.wireOp",EDGE,"E134"),sQuery(id+"F15.wireOp",EDGE,"E136"),sQuery(id+"F15.wireOp",EDGE,"E138"),sQuery(id+"F15.wireOp",EDGE,"E141"),sQuery(id+"F15.wireOp",EDGE,"E143"),sQuery(id+"F15.wireOp",EDGE,"E144"),sQuery(id+"F15.wireOp",EDGE,"E146"),sQuery(id+"F15.wireOp",EDGE,"E148"),sQuery(id+"F15.wireOp",EDGE,"E150")])]});
            var Q8;
            Q8=makeQuery(id+"F19.opExtrude","SWEPT_BODY",BODY,{"disambiguationData":[OSD([sQuery(id+"F18.wireOp",EDGE,"E152"),sQuery(id+"F18.wireOp",EDGE,"E154"),sQuery(id+"F18.wireOp",EDGE,"E156"),sQuery(id+"F18.wireOp",EDGE,"E159"),sQuery(id+"F18.wireOp",EDGE,"E161"),sQuery(id+"F18.wireOp",EDGE,"E163"),sQuery(id+"F18.wireOp",EDGE,"E165"),sQuery(id+"F18.wireOp",EDGE,"E166"),sQuery(id+"F18.wireOp",EDGE,"E168"),sQuery(id+"F18.wireOp",EDGE,"E171"),sQuery(id+"F18.wireOp",EDGE,"E173"),sQuery(id+"F18.wireOp",EDGE,"E175"),sQuery(id+"F18.wireOp",EDGE,"E177"),sQuery(id+"F18.wireOp",EDGE,"E179")])]});
            var Q9;
            Q9=makeQuery(id+"F19.opExtrude","SWEPT_BODY",BODY,{"disambiguationData":[OSD([sQuery(id+"F18.wireOp",EDGE,"E153"),sQuery(id+"F18.wireOp",EDGE,"E155"),sQuery(id+"F18.wireOp",EDGE,"E157"),sQuery(id+"F18.wireOp",EDGE,"E158"),sQuery(id+"F18.wireOp",EDGE,"E160"),sQuery(id+"F18.wireOp",EDGE,"E162"),sQuery(id+"F18.wireOp",EDGE,"E164"),sQuery(id+"F18.wireOp",EDGE,"E167"),sQuery(id+"F18.wireOp",EDGE,"E169"),sQuery(id+"F18.wireOp",EDGE,"E170"),sQuery(id+"F18.wireOp",EDGE,"E172"),sQuery(id+"F18.wireOp",EDGE,"E174"),sQuery(id+"F18.wireOp",EDGE,"E176"),sQuery(id+"F18.wireOp",EDGE,"E178")])]});
            var Q10;
            Q10=makeQuery(id+"F22.opExtrude","SWEPT_BODY",BODY,{"disambiguationData":[OSD([sQuery(id+"F21.wireOp",EDGE,"E180"),sQuery(id+"F21.wireOp",EDGE,"E183"),sQuery(id+"F21.wireOp",EDGE,"E185"),sQuery(id+"F21.wireOp",EDGE,"E186"),sQuery(id+"F21.wireOp",EDGE,"E188"),sQuery(id+"F21.wireOp",EDGE,"E190"),sQuery(id+"F21.wireOp",EDGE,"E192"),sQuery(id+"F21.wireOp",EDGE,"E194"),sQuery(id+"F21.wireOp",EDGE,"E196"),sQuery(id+"F21.wireOp",EDGE,"E199"),sQuery(id+"F21.wireOp",EDGE,"E201"),sQuery(id+"F21.wireOp",EDGE,"E203"),sQuery(id+"F21.wireOp",EDGE,"E204"),sQuery(id+"F21.wireOp",EDGE,"E206")])]});
            var Q11;
            Q11=makeQuery(id+"F22.opExtrude","SWEPT_BODY",BODY,{"disambiguationData":[OSD([sQuery(id+"F21.wireOp",EDGE,"E181"),sQuery(id+"F21.wireOp",EDGE,"E182"),sQuery(id+"F21.wireOp",EDGE,"E184"),sQuery(id+"F21.wireOp",EDGE,"E187"),sQuery(id+"F21.wireOp",EDGE,"E189"),sQuery(id+"F21.wireOp",EDGE,"E191"),sQuery(id+"F21.wireOp",EDGE,"E193"),sQuery(id+"F21.wireOp",EDGE,"E195"),sQuery(id+"F21.wireOp",EDGE,"E197"),sQuery(id+"F21.wireOp",EDGE,"E198"),sQuery(id+"F21.wireOp",EDGE,"E200"),sQuery(id+"F21.wireOp",EDGE,"E202"),sQuery(id+"F21.wireOp",EDGE,"E205"),sQuery(id+"F21.wireOp",EDGE,"E207")])]});
            var Q12;
            Q12=makeQuery(id+"F25.opExtrude","SWEPT_BODY",BODY,{"disambiguationData":[OSD([sQuery(id+"F24.wireOp",EDGE,"E208"),sQuery(id+"F24.wireOp",EDGE,"E210"),sQuery(id+"F24.wireOp",EDGE,"E212"),sQuery(id+"F24.wireOp",EDGE,"E215"),sQuery(id+"F24.wireOp",EDGE,"E217"),sQuery(id+"F24.wireOp",EDGE,"E219"),sQuery(id+"F24.wireOp",EDGE,"E221"),sQuery(id+"F24.wireOp",EDGE,"E223"),sQuery(id+"F24.wireOp",EDGE,"E224"),sQuery(id+"F24.wireOp",EDGE,"E226"),sQuery(id+"F24.wireOp",EDGE,"E229"),sQuery(id+"F24.wireOp",EDGE,"E231"),sQuery(id+"F24.wireOp",EDGE,"E233"),sQuery(id+"F24.wireOp",EDGE,"E235")])]});
            var Q13;
            Q13=makeQuery(id+"F25.opExtrude","SWEPT_BODY",BODY,{"disambiguationData":[OSD([sQuery(id+"F24.wireOp",EDGE,"E209"),sQuery(id+"F24.wireOp",EDGE,"E211"),sQuery(id+"F24.wireOp",EDGE,"E213"),sQuery(id+"F24.wireOp",EDGE,"E214"),sQuery(id+"F24.wireOp",EDGE,"E216"),sQuery(id+"F24.wireOp",EDGE,"E218"),sQuery(id+"F24.wireOp",EDGE,"E220"),sQuery(id+"F24.wireOp",EDGE,"E222"),sQuery(id+"F24.wireOp",EDGE,"E225"),sQuery(id+"F24.wireOp",EDGE,"E227"),sQuery(id+"F24.wireOp",EDGE,"E228"),sQuery(id+"F24.wireOp",EDGE,"E230"),sQuery(id+"F24.wireOp",EDGE,"E232"),sQuery(id+"F24.wireOp",EDGE,"E234")])]});
            var Q14;
            Q14=makeQuery(id+"F28.opExtrude","SWEPT_BODY",BODY,{"disambiguationData":[OSD([sQuery(id+"F27.wireOp",EDGE,"E240"),sQuery(id+"F27.wireOp",EDGE,"E242"),sQuery(id+"F27.wireOp",EDGE,"E244"),sQuery(id+"F27.wireOp",EDGE,"E246"),sQuery(id+"F27.wireOp",EDGE,"E248"),sQuery(id+"F27.wireOp",EDGE,"E251"),sQuery(id+"F27.wireOp",EDGE,"E253"),sQuery(id+"F27.wireOp",EDGE,"E254"),sQuery(id+"F27.wireOp",EDGE,"E256"),sQuery(id+"F27.wireOp",EDGE,"E258"),sQuery(id+"F27.wireOp",EDGE,"E260"),sQuery(id+"F27.wireOp",EDGE,"E263"),sQuery(id+"F27.wireOp",EDGE,"E267"),sQuery(id+"F27.wireOp",EDGE,"E265")])]});
            var Q15;
            Q15=makeQuery(id+"F28.opExtrude","SWEPT_BODY",BODY,{"disambiguationData":[OSD([sQuery(id+"F27.wireOp",EDGE,"E241"),sQuery(id+"F27.wireOp",EDGE,"E243"),sQuery(id+"F27.wireOp",EDGE,"E245"),sQuery(id+"F27.wireOp",EDGE,"E247"),sQuery(id+"F27.wireOp",EDGE,"E249"),sQuery(id+"F27.wireOp",EDGE,"E250"),sQuery(id+"F27.wireOp",EDGE,"E252"),sQuery(id+"F27.wireOp",EDGE,"E255"),sQuery(id+"F27.wireOp",EDGE,"E257"),sQuery(id+"F27.wireOp",EDGE,"E259"),sQuery(id+"F27.wireOp",EDGE,"E261"),sQuery(id+"F27.wireOp",EDGE,"E262"),sQuery(id+"F27.wireOp",EDGE,"E266"),sQuery(id+"F27.wireOp",EDGE,"E264")])]});
            var Q16;
            Q16=makeQuery(id+"F31.opExtrude","SWEPT_BODY",BODY,{"disambiguationData":[OSD([sQuery(id+"F30.wireOp",EDGE,"E268"),sQuery(id+"F30.wireOp",EDGE,"E271"),sQuery(id+"F30.wireOp",EDGE,"E272"),sQuery(id+"F30.wireOp",EDGE,"E274"),sQuery(id+"F30.wireOp",EDGE,"E277"),sQuery(id+"F30.wireOp",EDGE,"E279"),sQuery(id+"F30.wireOp",EDGE,"E281"),sQuery(id+"F30.wireOp",EDGE,"E283"),sQuery(id+"F30.wireOp",EDGE,"E284"),sQuery(id+"F30.wireOp",EDGE,"E286"),sQuery(id+"F30.wireOp",EDGE,"E289"),sQuery(id+"F30.wireOp",EDGE,"E291"),sQuery(id+"F30.wireOp",EDGE,"E293"),sQuery(id+"F30.wireOp",EDGE,"E295")])]});
            var Q17;
            Q17=makeQuery(id+"F31.opExtrude","SWEPT_BODY",BODY,{"disambiguationData":[OSD([sQuery(id+"F30.wireOp",EDGE,"E269"),sQuery(id+"F30.wireOp",EDGE,"E270"),sQuery(id+"F30.wireOp",EDGE,"E273"),sQuery(id+"F30.wireOp",EDGE,"E275"),sQuery(id+"F30.wireOp",EDGE,"E276"),sQuery(id+"F30.wireOp",EDGE,"E278"),sQuery(id+"F30.wireOp",EDGE,"E280"),sQuery(id+"F30.wireOp",EDGE,"E282"),sQuery(id+"F30.wireOp",EDGE,"E285"),sQuery(id+"F30.wireOp",EDGE,"E287"),sQuery(id+"F30.wireOp",EDGE,"E288"),sQuery(id+"F30.wireOp",EDGE,"E290"),sQuery(id+"F30.wireOp",EDGE,"E292"),sQuery(id+"F30.wireOp",EDGE,"E294")])]});
            var Q18;
            Q18=makeQuery(id+"F34.opExtrude","SWEPT_BODY",BODY,{"disambiguationData":[OSD([sQuery(id+"F33.wireOp",EDGE,"E296"),sQuery(id+"F33.wireOp",EDGE,"E298"),sQuery(id+"F33.wireOp",EDGE,"E300"),sQuery(id+"F33.wireOp",EDGE,"E302"),sQuery(id+"F33.wireOp",EDGE,"E305"),sQuery(id+"F33.wireOp",EDGE,"E307"),sQuery(id+"F33.wireOp",EDGE,"E308"),sQuery(id+"F33.wireOp",EDGE,"E310"),sQuery(id+"F33.wireOp",EDGE,"E312"),sQuery(id+"F33.wireOp",EDGE,"E314"),sQuery(id+"F33.wireOp",EDGE,"E316"),sQuery(id+"F33.wireOp",EDGE,"E319"),sQuery(id+"F33.wireOp",EDGE,"E321"),sQuery(id+"F33.wireOp",EDGE,"E323")])]});
            var Q19;
            Q19=makeQuery(id+"F34.opExtrude","SWEPT_BODY",BODY,{"disambiguationData":[OSD([sQuery(id+"F33.wireOp",EDGE,"E297"),sQuery(id+"F33.wireOp",EDGE,"E299"),sQuery(id+"F33.wireOp",EDGE,"E301"),sQuery(id+"F33.wireOp",EDGE,"E303"),sQuery(id+"F33.wireOp",EDGE,"E304"),sQuery(id+"F33.wireOp",EDGE,"E306"),sQuery(id+"F33.wireOp",EDGE,"E309"),sQuery(id+"F33.wireOp",EDGE,"E311"),sQuery(id+"F33.wireOp",EDGE,"E313"),sQuery(id+"F33.wireOp",EDGE,"E315"),sQuery(id+"F33.wireOp",EDGE,"E317"),sQuery(id+"F33.wireOp",EDGE,"E318"),sQuery(id+"F33.wireOp",EDGE,"E320"),sQuery(id+"F33.wireOp",EDGE,"E322")])]});
            var Q20;
            Q20=makeQuery(id+"F46.opPattern","COPY",BODY,{"derivedFrom":makeQuery(id+"F7.opExtrude","SWEPT_BODY",BODY,{"disambiguationData":[OSD([sQuery(id+"F6.wireOp",EDGE,"E56"),sQuery(id+"F6.wireOp",EDGE,"E57"),sQuery(id+"F6.wireOp",EDGE,"E58"),sQuery(id+"F6.wireOp",EDGE,"E59"),sQuery(id+"F6.wireOp",EDGE,"E60"),sQuery(id+"F6.wireOp",EDGE,"E61"),sQuery(id+"F6.wireOp",EDGE,"E62"),sQuery(id+"F6.wireOp",EDGE,"E63"),sQuery(id+"F6.wireOp",EDGE,"E64"),sQuery(id+"F6.wireOp",EDGE,"E65"),sQuery(id+"F6.wireOp",EDGE,"E66"),sQuery(id+"F6.wireOp",EDGE,"E67")])]}),"instanceName":"1"});
            var Q21;
            Q21=makeQuery(id+"F46.opPattern","COPY",BODY,{"derivedFrom":makeQuery(id+"F7.opExtrude","SWEPT_BODY",BODY,{"disambiguationData":[OSD([sQuery(id+"F6.wireOp",EDGE,"E56"),sQuery(id+"F6.wireOp",EDGE,"E57"),sQuery(id+"F6.wireOp",EDGE,"E58"),sQuery(id+"F6.wireOp",EDGE,"E59"),sQuery(id+"F6.wireOp",EDGE,"E60"),sQuery(id+"F6.wireOp",EDGE,"E61"),sQuery(id+"F6.wireOp",EDGE,"E62"),sQuery(id+"F6.wireOp",EDGE,"E63"),sQuery(id+"F6.wireOp",EDGE,"E64"),sQuery(id+"F6.wireOp",EDGE,"E65"),sQuery(id+"F6.wireOp",EDGE,"E66"),sQuery(id+"F6.wireOp",EDGE,"E67")])]}),"instanceName":"2"});
            var Q22;
            Q22=makeQuery(id+"F46.opPattern","COPY",BODY,{"derivedFrom":makeQuery(id+"F7.opExtrude","SWEPT_BODY",BODY,{"disambiguationData":[OSD([sQuery(id+"F6.wireOp",EDGE,"E56"),sQuery(id+"F6.wireOp",EDGE,"E57"),sQuery(id+"F6.wireOp",EDGE,"E58"),sQuery(id+"F6.wireOp",EDGE,"E59"),sQuery(id+"F6.wireOp",EDGE,"E60"),sQuery(id+"F6.wireOp",EDGE,"E61"),sQuery(id+"F6.wireOp",EDGE,"E62"),sQuery(id+"F6.wireOp",EDGE,"E63"),sQuery(id+"F6.wireOp",EDGE,"E64"),sQuery(id+"F6.wireOp",EDGE,"E65"),sQuery(id+"F6.wireOp",EDGE,"E66"),sQuery(id+"F6.wireOp",EDGE,"E67")])]}),"instanceName":"3"});
            var Q23;
            Q23=makeQuery(id+"F46.opPattern","COPY",BODY,{"derivedFrom":makeQuery(id+"F7.opExtrude","SWEPT_BODY",BODY,{"disambiguationData":[OSD([sQuery(id+"F6.wireOp",EDGE,"E56"),sQuery(id+"F6.wireOp",EDGE,"E57"),sQuery(id+"F6.wireOp",EDGE,"E58"),sQuery(id+"F6.wireOp",EDGE,"E59"),sQuery(id+"F6.wireOp",EDGE,"E60"),sQuery(id+"F6.wireOp",EDGE,"E61"),sQuery(id+"F6.wireOp",EDGE,"E62"),sQuery(id+"F6.wireOp",EDGE,"E63"),sQuery(id+"F6.wireOp",EDGE,"E64"),sQuery(id+"F6.wireOp",EDGE,"E65"),sQuery(id+"F6.wireOp",EDGE,"E66"),sQuery(id+"F6.wireOp",EDGE,"E67")])]}),"instanceName":"4"});
            var Q24;
            Q24=makeQuery(id+"F46.opPattern","COPY",BODY,{"derivedFrom":makeQuery(id+"F7.opExtrude","SWEPT_BODY",BODY,{"disambiguationData":[OSD([sQuery(id+"F6.wireOp",EDGE,"E56"),sQuery(id+"F6.wireOp",EDGE,"E57"),sQuery(id+"F6.wireOp",EDGE,"E58"),sQuery(id+"F6.wireOp",EDGE,"E59"),sQuery(id+"F6.wireOp",EDGE,"E60"),sQuery(id+"F6.wireOp",EDGE,"E61"),sQuery(id+"F6.wireOp",EDGE,"E62"),sQuery(id+"F6.wireOp",EDGE,"E63"),sQuery(id+"F6.wireOp",EDGE,"E64"),sQuery(id+"F6.wireOp",EDGE,"E65"),sQuery(id+"F6.wireOp",EDGE,"E66"),sQuery(id+"F6.wireOp",EDGE,"E67")])]}),"instanceName":"5"});
            var Q25;
            Q25=makeQuery(id+"F46.opPattern","COPY",BODY,{"derivedFrom":makeQuery(id+"F7.opExtrude","SWEPT_BODY",BODY,{"disambiguationData":[OSD([sQuery(id+"F6.wireOp",EDGE,"E56"),sQuery(id+"F6.wireOp",EDGE,"E57"),sQuery(id+"F6.wireOp",EDGE,"E58"),sQuery(id+"F6.wireOp",EDGE,"E59"),sQuery(id+"F6.wireOp",EDGE,"E60"),sQuery(id+"F6.wireOp",EDGE,"E61"),sQuery(id+"F6.wireOp",EDGE,"E62"),sQuery(id+"F6.wireOp",EDGE,"E63"),sQuery(id+"F6.wireOp",EDGE,"E64"),sQuery(id+"F6.wireOp",EDGE,"E65"),sQuery(id+"F6.wireOp",EDGE,"E66"),sQuery(id+"F6.wireOp",EDGE,"E67")])]}),"instanceName":"6"});
            var Q26;
            Q26=makeQuery(id+"F46.opPattern","COPY",BODY,{"derivedFrom":makeQuery(id+"F7.opExtrude","SWEPT_BODY",BODY,{"disambiguationData":[OSD([sQuery(id+"F6.wireOp",EDGE,"E56"),sQuery(id+"F6.wireOp",EDGE,"E57"),sQuery(id+"F6.wireOp",EDGE,"E58"),sQuery(id+"F6.wireOp",EDGE,"E59"),sQuery(id+"F6.wireOp",EDGE,"E60"),sQuery(id+"F6.wireOp",EDGE,"E61"),sQuery(id+"F6.wireOp",EDGE,"E62"),sQuery(id+"F6.wireOp",EDGE,"E63"),sQuery(id+"F6.wireOp",EDGE,"E64"),sQuery(id+"F6.wireOp",EDGE,"E65"),sQuery(id+"F6.wireOp",EDGE,"E66"),sQuery(id+"F6.wireOp",EDGE,"E67")])]}),"instanceName":"7"});
            var Q27;
            Q27=makeQuery(id+"F46.opPattern","COPY",BODY,{"derivedFrom":makeQuery(id+"F7.opExtrude","SWEPT_BODY",BODY,{"disambiguationData":[OSD([sQuery(id+"F6.wireOp",EDGE,"E56"),sQuery(id+"F6.wireOp",EDGE,"E57"),sQuery(id+"F6.wireOp",EDGE,"E58"),sQuery(id+"F6.wireOp",EDGE,"E59"),sQuery(id+"F6.wireOp",EDGE,"E60"),sQuery(id+"F6.wireOp",EDGE,"E61"),sQuery(id+"F6.wireOp",EDGE,"E62"),sQuery(id+"F6.wireOp",EDGE,"E63"),sQuery(id+"F6.wireOp",EDGE,"E64"),sQuery(id+"F6.wireOp",EDGE,"E65"),sQuery(id+"F6.wireOp",EDGE,"E66"),sQuery(id+"F6.wireOp",EDGE,"E67")])]}),"instanceName":"8"});
            var Q28;
            Q28=makeQuery(id+"F46.opPattern","COPY",BODY,{"derivedFrom":makeQuery(id+"F7.opExtrude","SWEPT_BODY",BODY,{"disambiguationData":[OSD([sQuery(id+"F6.wireOp",EDGE,"E56"),sQuery(id+"F6.wireOp",EDGE,"E57"),sQuery(id+"F6.wireOp",EDGE,"E58"),sQuery(id+"F6.wireOp",EDGE,"E59"),sQuery(id+"F6.wireOp",EDGE,"E60"),sQuery(id+"F6.wireOp",EDGE,"E61"),sQuery(id+"F6.wireOp",EDGE,"E62"),sQuery(id+"F6.wireOp",EDGE,"E63"),sQuery(id+"F6.wireOp",EDGE,"E64"),sQuery(id+"F6.wireOp",EDGE,"E65"),sQuery(id+"F6.wireOp",EDGE,"E66"),sQuery(id+"F6.wireOp",EDGE,"E67")])]}),"instanceName":"9"});
            var Q29;
            Q29=makeQuery(id+"F46.opPattern","COPY",BODY,{"derivedFrom":makeQuery(id+"F7.opExtrude","SWEPT_BODY",BODY,{"disambiguationData":[OSD([sQuery(id+"F6.wireOp",EDGE,"E56"),sQuery(id+"F6.wireOp",EDGE,"E57"),sQuery(id+"F6.wireOp",EDGE,"E58"),sQuery(id+"F6.wireOp",EDGE,"E59"),sQuery(id+"F6.wireOp",EDGE,"E60"),sQuery(id+"F6.wireOp",EDGE,"E61"),sQuery(id+"F6.wireOp",EDGE,"E62"),sQuery(id+"F6.wireOp",EDGE,"E63"),sQuery(id+"F6.wireOp",EDGE,"E64"),sQuery(id+"F6.wireOp",EDGE,"E65"),sQuery(id+"F6.wireOp",EDGE,"E66"),sQuery(id+"F6.wireOp",EDGE,"E67")])]}),"instanceName":"10"});
            var Q30;
            Q30=makeQuery(id+"F46.opPattern","COPY",BODY,{"derivedFrom":makeQuery(id+"F7.opExtrude","SWEPT_BODY",BODY,{"disambiguationData":[OSD([sQuery(id+"F6.wireOp",EDGE,"E56"),sQuery(id+"F6.wireOp",EDGE,"E57"),sQuery(id+"F6.wireOp",EDGE,"E58"),sQuery(id+"F6.wireOp",EDGE,"E59"),sQuery(id+"F6.wireOp",EDGE,"E60"),sQuery(id+"F6.wireOp",EDGE,"E61"),sQuery(id+"F6.wireOp",EDGE,"E62"),sQuery(id+"F6.wireOp",EDGE,"E63"),sQuery(id+"F6.wireOp",EDGE,"E64"),sQuery(id+"F6.wireOp",EDGE,"E65"),sQuery(id+"F6.wireOp",EDGE,"E66"),sQuery(id+"F6.wireOp",EDGE,"E67")])]}),"instanceName":"11"});
            var Q31;
            Q31=makeQuery(id+"F46.opPattern","COPY",BODY,{"derivedFrom":makeQuery(id+"F7.opExtrude","SWEPT_BODY",BODY,{"disambiguationData":[OSD([sQuery(id+"F6.wireOp",EDGE,"E56"),sQuery(id+"F6.wireOp",EDGE,"E57"),sQuery(id+"F6.wireOp",EDGE,"E58"),sQuery(id+"F6.wireOp",EDGE,"E59"),sQuery(id+"F6.wireOp",EDGE,"E60"),sQuery(id+"F6.wireOp",EDGE,"E61"),sQuery(id+"F6.wireOp",EDGE,"E62"),sQuery(id+"F6.wireOp",EDGE,"E63"),sQuery(id+"F6.wireOp",EDGE,"E64"),sQuery(id+"F6.wireOp",EDGE,"E65"),sQuery(id+"F6.wireOp",EDGE,"E66"),sQuery(id+"F6.wireOp",EDGE,"E67")])]}),"instanceName":"12"});
            var Q32;
            Q32=makeQuery(id+"F46.opPattern","COPY",BODY,{"derivedFrom":makeQuery(id+"F7.opExtrude","SWEPT_BODY",BODY,{"disambiguationData":[OSD([sQuery(id+"F6.wireOp",EDGE,"E56"),sQuery(id+"F6.wireOp",EDGE,"E57"),sQuery(id+"F6.wireOp",EDGE,"E58"),sQuery(id+"F6.wireOp",EDGE,"E59"),sQuery(id+"F6.wireOp",EDGE,"E60"),sQuery(id+"F6.wireOp",EDGE,"E61"),sQuery(id+"F6.wireOp",EDGE,"E62"),sQuery(id+"F6.wireOp",EDGE,"E63"),sQuery(id+"F6.wireOp",EDGE,"E64"),sQuery(id+"F6.wireOp",EDGE,"E65"),sQuery(id+"F6.wireOp",EDGE,"E66"),sQuery(id+"F6.wireOp",EDGE,"E67")])]}),"instanceName":"13"});
            var Q33;
            Q33=makeQuery(id+"F46.opPattern","COPY",BODY,{"derivedFrom":makeQuery(id+"F7.opExtrude","SWEPT_BODY",BODY,{"disambiguationData":[OSD([sQuery(id+"F6.wireOp",EDGE,"E56"),sQuery(id+"F6.wireOp",EDGE,"E57"),sQuery(id+"F6.wireOp",EDGE,"E58"),sQuery(id+"F6.wireOp",EDGE,"E59"),sQuery(id+"F6.wireOp",EDGE,"E60"),sQuery(id+"F6.wireOp",EDGE,"E61"),sQuery(id+"F6.wireOp",EDGE,"E62"),sQuery(id+"F6.wireOp",EDGE,"E63"),sQuery(id+"F6.wireOp",EDGE,"E64"),sQuery(id+"F6.wireOp",EDGE,"E65"),sQuery(id+"F6.wireOp",EDGE,"E66"),sQuery(id+"F6.wireOp",EDGE,"E67")])]}),"instanceName":"14"});
            var Q34;
            Q34=makeQuery(id+"F46.opPattern","COPY",BODY,{"derivedFrom":makeQuery(id+"F7.opExtrude","SWEPT_BODY",BODY,{"disambiguationData":[OSD([sQuery(id+"F6.wireOp",EDGE,"E56"),sQuery(id+"F6.wireOp",EDGE,"E57"),sQuery(id+"F6.wireOp",EDGE,"E58"),sQuery(id+"F6.wireOp",EDGE,"E59"),sQuery(id+"F6.wireOp",EDGE,"E60"),sQuery(id+"F6.wireOp",EDGE,"E61"),sQuery(id+"F6.wireOp",EDGE,"E62"),sQuery(id+"F6.wireOp",EDGE,"E63"),sQuery(id+"F6.wireOp",EDGE,"E64"),sQuery(id+"F6.wireOp",EDGE,"E65"),sQuery(id+"F6.wireOp",EDGE,"E66"),sQuery(id+"F6.wireOp",EDGE,"E67")])]}),"instanceName":"15"});
            var Q35;
            Q35=makeQuery(id+"F46.opPattern","COPY",BODY,{"derivedFrom":makeQuery(id+"F7.opExtrude","SWEPT_BODY",BODY,{"disambiguationData":[OSD([sQuery(id+"F6.wireOp",EDGE,"E56"),sQuery(id+"F6.wireOp",EDGE,"E57"),sQuery(id+"F6.wireOp",EDGE,"E58"),sQuery(id+"F6.wireOp",EDGE,"E59"),sQuery(id+"F6.wireOp",EDGE,"E60"),sQuery(id+"F6.wireOp",EDGE,"E61"),sQuery(id+"F6.wireOp",EDGE,"E62"),sQuery(id+"F6.wireOp",EDGE,"E63"),sQuery(id+"F6.wireOp",EDGE,"E64"),sQuery(id+"F6.wireOp",EDGE,"E65"),sQuery(id+"F6.wireOp",EDGE,"E66"),sQuery(id+"F6.wireOp",EDGE,"E67")])]}),"instanceName":"16"});
            var Q36;
            Q36=makeQuery(id+"F46.opPattern","COPY",BODY,{"derivedFrom":makeQuery(id+"F7.opExtrude","SWEPT_BODY",BODY,{"disambiguationData":[OSD([sQuery(id+"F6.wireOp",EDGE,"E56"),sQuery(id+"F6.wireOp",EDGE,"E57"),sQuery(id+"F6.wireOp",EDGE,"E58"),sQuery(id+"F6.wireOp",EDGE,"E59"),sQuery(id+"F6.wireOp",EDGE,"E60"),sQuery(id+"F6.wireOp",EDGE,"E61"),sQuery(id+"F6.wireOp",EDGE,"E62"),sQuery(id+"F6.wireOp",EDGE,"E63"),sQuery(id+"F6.wireOp",EDGE,"E64"),sQuery(id+"F6.wireOp",EDGE,"E65"),sQuery(id+"F6.wireOp",EDGE,"E66"),sQuery(id+"F6.wireOp",EDGE,"E67")])]}),"instanceName":"17"});
            var Q37;
            Q37=makeQuery(id+"F46.opPattern","COPY",BODY,{"derivedFrom":makeQuery(id+"F7.opExtrude","SWEPT_BODY",BODY,{"disambiguationData":[OSD([sQuery(id+"F6.wireOp",EDGE,"E56"),sQuery(id+"F6.wireOp",EDGE,"E57"),sQuery(id+"F6.wireOp",EDGE,"E58"),sQuery(id+"F6.wireOp",EDGE,"E59"),sQuery(id+"F6.wireOp",EDGE,"E60"),sQuery(id+"F6.wireOp",EDGE,"E61"),sQuery(id+"F6.wireOp",EDGE,"E62"),sQuery(id+"F6.wireOp",EDGE,"E63"),sQuery(id+"F6.wireOp",EDGE,"E64"),sQuery(id+"F6.wireOp",EDGE,"E65"),sQuery(id+"F6.wireOp",EDGE,"E66"),sQuery(id+"F6.wireOp",EDGE,"E67")])]}),"instanceName":"18"});
            var Q38;
            Q38=makeQuery(id+"F46.opPattern","COPY",BODY,{"derivedFrom":makeQuery(id+"F7.opExtrude","SWEPT_BODY",BODY,{"disambiguationData":[OSD([sQuery(id+"F6.wireOp",EDGE,"E56"),sQuery(id+"F6.wireOp",EDGE,"E57"),sQuery(id+"F6.wireOp",EDGE,"E58"),sQuery(id+"F6.wireOp",EDGE,"E59"),sQuery(id+"F6.wireOp",EDGE,"E60"),sQuery(id+"F6.wireOp",EDGE,"E61"),sQuery(id+"F6.wireOp",EDGE,"E62"),sQuery(id+"F6.wireOp",EDGE,"E63"),sQuery(id+"F6.wireOp",EDGE,"E64"),sQuery(id+"F6.wireOp",EDGE,"E65"),sQuery(id+"F6.wireOp",EDGE,"E66"),sQuery(id+"F6.wireOp",EDGE,"E67")])]}),"instanceName":"19"});
            var Q39;
            Q39=makeQuery(id+"F7.opExtrude","SWEPT_BODY",BODY,{"disambiguationData":[OSD([sQuery(id+"F6.wireOp",EDGE,"E56"),sQuery(id+"F6.wireOp",EDGE,"E57"),sQuery(id+"F6.wireOp",EDGE,"E58"),sQuery(id+"F6.wireOp",EDGE,"E59"),sQuery(id+"F6.wireOp",EDGE,"E60"),sQuery(id+"F6.wireOp",EDGE,"E61"),sQuery(id+"F6.wireOp",EDGE,"E62"),sQuery(id+"F6.wireOp",EDGE,"E63"),sQuery(id+"F6.wireOp",EDGE,"E64"),sQuery(id+"F6.wireOp",EDGE,"E65"),sQuery(id+"F6.wireOp",EDGE,"E66"),sQuery(id+"F6.wireOp",EDGE,"E67")])]});
            var Q40;
            Q40=makeQuery(id+"F39.opExtrude","SWEPT_BODY",BODY,{"disambiguationData":[OSD([sQuery(id+"F38.wireOp",EDGE,"E328"),sQuery(id+"F38.wireOp",EDGE,"or8u7yw1-5iI8-fih6-ifgH-aQ84WTj8Eifl")])]});
            var Q41;
            Q41=makeQuery(id+"F36.opExtrude","SWEPT_BODY",BODY,{"disambiguationData":[OSD([sQuery(id+"F35.wireOp",EDGE,"E324"),sQuery(id+"F35.wireOp",EDGE,"E325")])]});
            var Q42;
            Q42=makeQuery(id+"F42.opExtrude","SWEPT_BODY",BODY,{"disambiguationData":[OSD([sQuery(id+"F41.wireOp",EDGE,"E334"),sQuery(id+"F41.wireOp",EDGE,"E335")])]});
            var Q43;
            Q43=makeQuery(id+"F45.opExtrude","SWEPT_BODY",BODY,{"disambiguationData":[OSD([sQuery(id+"F44.wireOp",EDGE,"E338"),sQuery(id+"F44.wireOp",EDGE,"E340")])]});
            var Q44;
            Q44=makeQuery(id+"F52.opExtrude","SWEPT_BODY",BODY,{"disambiguationData":[OSD([sQuery(id+"F51.wireOp",EDGE,"E349.0"),sQuery(id+"F51.wireOp",EDGE,"E350")])]});
            var Q45;
            Q45=makeQuery(id+"F49.opExtrude","SWEPT_BODY",BODY,{"disambiguationData":[OSD([sQuery(id+"F48.wireOp",EDGE,"E342.0"),sQuery(id+"F48.wireOp",EDGE,"E343")])]});
            booleanBodies(context, id + "F54", {"operationType" : BooleanOperationType.SUBTRACTION, "tools" : qUnion([Q0, Q1, Q2, Q3, Q4, Q5, Q6, Q7, Q8, Q9, Q10, Q11, Q12, Q13, Q14, Q15, Q16, Q17, Q18, Q19, Q20, Q21, Q22, Q23, Q24, Q25, Q26, Q27, Q28, Q29, Q30, Q31, Q32, Q33, Q34, Q35, Q36, Q37, Q38, Q39]), "targets" : qUnion([Q40, Q41, Q42, Q43, Q44, Q45]), "keepTools" : true});
        }
        {
            var Q0;
            Q0=qCreatedBy(makeId("Front.planeOp"),FACE);
            var sketch = newSketch(context, id + "F55", { "sketchPlane" : qUnion([Q0])});
            skLineSegment(sketch, "E351", {"start": v(0, 198.88) * mm, "end": v(14, 198.88) * mm});
            skLineSegment(sketch, "E352", {"start": v(14, 198.88) * mm, "end": v(14, 170.38) * mm});
            skLineSegment(sketch, "E353", {"start": v(14, 170.38) * mm, "end": v(23, 152.88) * mm, "construction": true});
            skLineSegment(sketch, "E354", {"start": v(23, 152.88) * mm, "end": v(23, 139.88) * mm});
            skLineSegment(sketch, "E355", {"start": v(23, 139.88) * mm, "end": v(25, 139.88) * mm});
            skLineSegment(sketch, "E356", {"start": v(25, 139.88) * mm, "end": v(25, 137.88) * mm});
            skLineSegment(sketch, "E357", {"start": v(25, 137.88) * mm, "end": v(0, 137.88) * mm});
            skLineSegment(sketch, "E358", {"start": v(0, 137.88) * mm, "end": v(0, 198.88) * mm});
            skArc(sketch, "E359", {"start": v(23, 152.88) * mm, "mid": v(20.62, 162.71) * mm, "end": v(14, 170.38) * mm});
            skSolve(sketch);
        }
        {
            var Q0;
            Q0 = qSketchRegion(id + "F55", true);
            var Q1;
            Q1=sQuery(id+"F55.wireOp",EDGE,"E358");
            revolve(context, id + "F56", {"surfaceOperationType" : NewSurfaceOperationType.NEW, "entities" : qUnion([Q0]), "axis" : qUnion([Q1]), "revolveType" : RevolveType.FULL});
        }
    });
